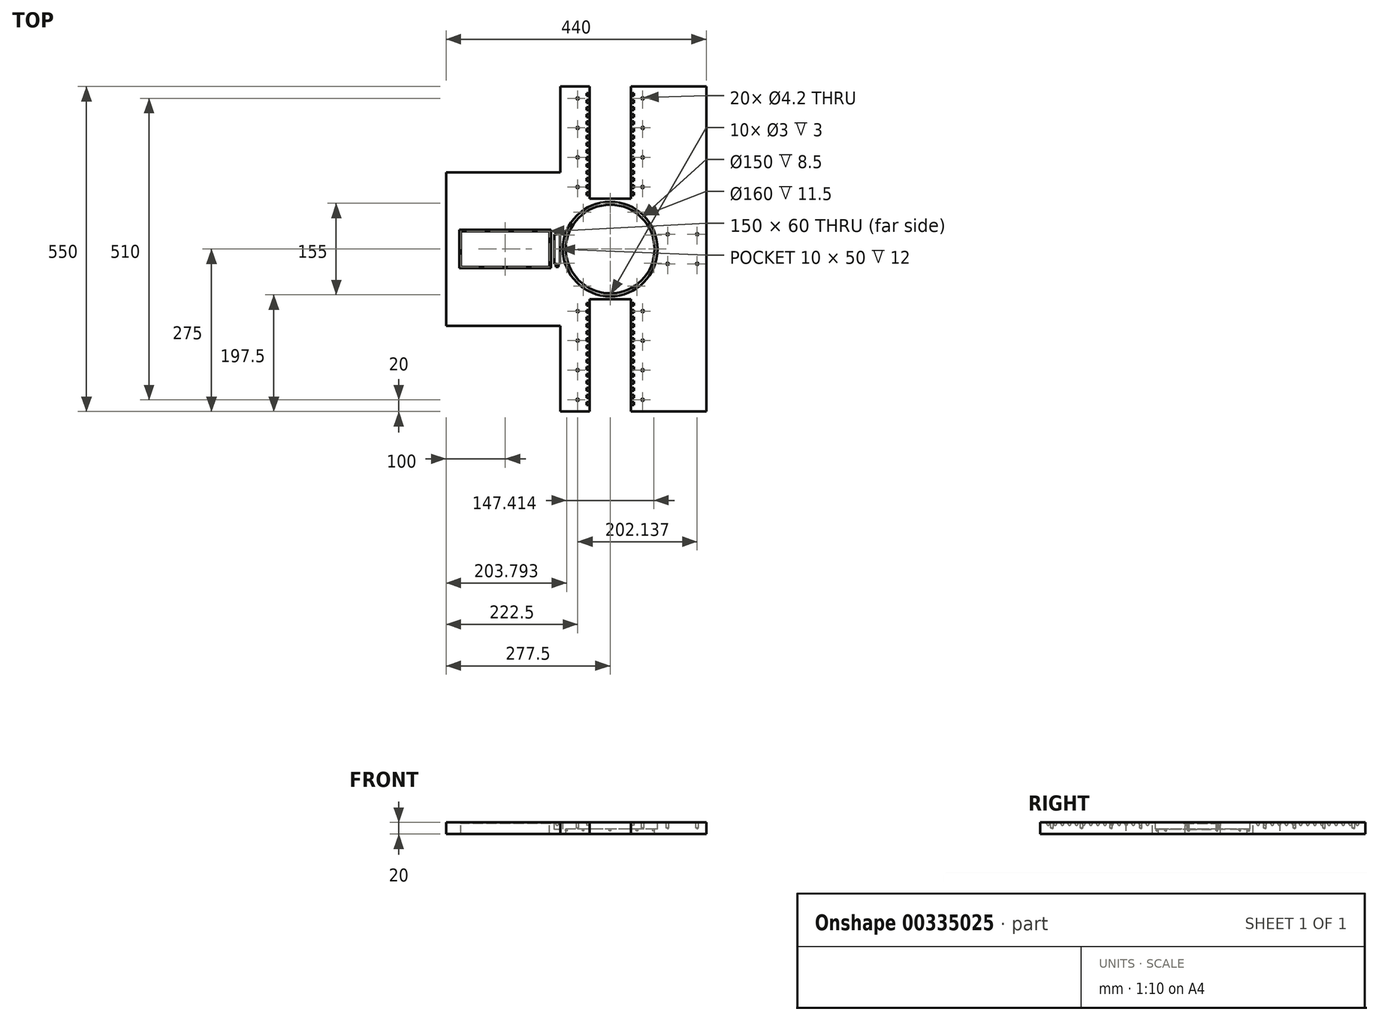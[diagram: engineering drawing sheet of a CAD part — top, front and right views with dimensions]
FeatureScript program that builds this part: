
annotation { "Feature Type Name" : "Feature", "Feature Type Description" : "" }
export const myFeature = defineFeature(function(context is Context, id is Id, definition is map)
    precondition{}
    {
        {
            var Q0;
            Q0=qCreatedBy(makeId("Top.planeOp"),FACE);
            var sketch = newSketch(context, id + "F0", { "sketchPlane" : qUnion([Q0])});
            skLineSegment(sketch, "E0.bottom", {"start": v(100, -127.5) * mm, "end": v(-100, -127.5) * mm});
            skLineSegment(sketch, "E0.top", {"start": v(100, 127.5) * mm, "end": v(-100, 127.5) * mm});
            skLineSegment(sketch, "E0.left", {"start": v(100, -127.5) * mm, "end": v(100, 127.5) * mm});
            skLineSegment(sketch, "E0.right", {"start": v(-100, -127.5) * mm, "end": v(-100, 127.5) * mm});
            skPoint(sketch, "E0.middle", {"position": v(0, 0) * mm});
            skSolve(sketch);
        }
        {
            var Q0;
            Q0 = qSketchRegion(id + "F0", true);
            extrude(context, id + "F1", {"entities" : qUnion([Q0]), "depth" : 20 * mm});
        }
        {
            var Q0;
            Q0=makeQuery(id+"F1.opExtrude","CAP_FACE",FACE,{"disambiguationData":[OSD([sQuery(id+"F0.wireOp",EDGE,"E0.bottom"),sQuery(id+"F0.wireOp",EDGE,"E0.top"),sQuery(id+"F0.wireOp",EDGE,"E0.left"),sQuery(id+"F0.wireOp",EDGE,"E0.right")])],"isStart":false});
            var sketch = newSketch(context, id + "F2", { "sketchPlane" : qUnion([Q0])});
            skLineSegment(sketch, "E1.bottom", {"start": v(75, -30) * mm, "end": v(-75, -30) * mm});
            skLineSegment(sketch, "E1.top", {"start": v(75, 30) * mm, "end": v(-75, 30) * mm});
            skLineSegment(sketch, "E1.left", {"start": v(75, -30) * mm, "end": v(75, 30) * mm});
            skLineSegment(sketch, "E1.right", {"start": v(-75, -30) * mm, "end": v(-75, 30) * mm});
            skPoint(sketch, "E1.middle", {"position": v(0, 0) * mm});
            skSolve(sketch);
        }
        {
            var Q0;
            Q0=makeQuery(id+"F2.imprint","IMPRINT",FACE,{"disambiguationData":[TD([[makeQuery(id+"F2.imprint","IMPRINT",EDGE,{"derivedFrom":sQuery(id+"F2.wireOp",EDGE,"E1.bottom")}),-1.0]])]});
            extrude(context, id + "F3", {"entities" : qUnion([Q0]), "operationType" : NewBodyOperationType.REMOVE, "endBound" : BoundingType.THROUGH_ALL, "oppositeDirection" : true, "depth" : 25 * mm});
        }
        {
            var Q0;
            Q0=makeQuery(id+"F1.opExtrude","CAP_FACE",FACE,{"disambiguationData":[OSD([sQuery(id+"F0.wireOp",EDGE,"E0.bottom"),sQuery(id+"F0.wireOp",EDGE,"E0.top"),sQuery(id+"F0.wireOp",EDGE,"E0.left"),sQuery(id+"F0.wireOp",EDGE,"E0.right")])],"isStart":false});
            var sketch = newSketch(context, id + "F4", { "sketchPlane" : qUnion([Q0])});
            skLineSegment(sketch, "E2.bottom", {"start": v(77.5, -32.5) * mm, "end": v(-77.5, -32.5) * mm});
            skLineSegment(sketch, "E2.top", {"start": v(77.5, 32.5) * mm, "end": v(-77.5, 32.5) * mm});
            skLineSegment(sketch, "E2.left", {"start": v(77.5, -32.5) * mm, "end": v(77.5, 32.5) * mm});
            skLineSegment(sketch, "E2.right", {"start": v(-77.5, -32.5) * mm, "end": v(-77.5, 32.5) * mm});
            skPoint(sketch, "E2.middle", {"position": v(0, 0) * mm});
            skSolve(sketch);
        }
        {
            var Q0;
            Q0=makeQuery(id+"F4.imprint","IMPRINT",FACE,{"disambiguationData":[TD([[makeQuery(id+"F4.imprint","IMPRINT",EDGE,{"derivedFrom":sQuery(id+"F4.wireOp",EDGE,"E2.bottom")}),-1.0]])]});
            extrude(context, id + "F5", {"entities" : qUnion([Q0]), "operationType" : NewBodyOperationType.REMOVE, "oppositeDirection" : true, "depth" : 2 * mm});
        }
        {
            var Q0;
            Q0=makeQuery(id+"F1.opExtrude","SWEPT_FACE",FACE,{"disambiguationData":[OSD([sQuery(id+"F0.wireOp",EDGE,"E0.left")])]});
            extrude(context, id + "F6", {"entities" : qUnion([Q0]), "operationType" : NewBodyOperationType.ADD, "depth" : 240 * mm});
        }
        {
            var Q0;
            {var subQ0=sQuery(id+"F0.wireOp",EDGE,"E0.left");Q0=makeQuery(id+"F6.boolean.opBoolean","MERGE",FACE,{"derivedFrom":[makeQuery(id+"F1.opExtrude","CAP_FACE",FACE,{"disambiguationData":[OSD([sQuery(id+"F0.wireOp",EDGE,"E0.bottom"),sQuery(id+"F0.wireOp",EDGE,"E0.top"),subQ0,sQuery(id+"F0.wireOp",EDGE,"E0.right")])],"isStart":false}),makeQuery(id+"F6.opExtrude","SWEPT_FACE",FACE,{"disambiguationData":[OSD([subQ0]),TDD([makeQuery(id+"F1.opExtrude","CAP_EDGE",EDGE,{"disambiguationData":[OSD([subQ0])],"isStart":false})])]})]});}
            var sketch = newSketch(context, id + "F7", { "sketchPlane" : qUnion([Q0])});
            skCircle(sketch, "E3", {"center": v(177.5, 0) * mm, "radius": 80 * mm});
            skCircle(sketch, "E4", {"center": v(177.5, 0) * mm, "radius": 75 * mm});
            skSolve(sketch);
        }
        {
            var Q0;
            Q0=makeQuery(id+"F7.imprint","IMPRINT",FACE,{"disambiguationData":[TD([[makeQuery(id+"F7.imprint","IMPRINT",EDGE,{"derivedFrom":sQuery(id+"F7.wireOp",EDGE,"E4")}),1.0]])]});
            extrude(context, id + "F8", {"entities" : qUnion([Q0]), "operationType" : NewBodyOperationType.REMOVE, "oppositeDirection" : true, "depth" : 25 * mm});
        }
        {
            var Q0;
            Q0 = qSketchRegion(id + "F7", true);
            extrude(context, id + "F9", {"entities" : qUnion([Q0]), "operationType" : NewBodyOperationType.REMOVE, "oppositeDirection" : true, "depth" : 11.5 * mm});
        }
        {
            var Q0;
            {var subQ0=sQuery(id+"F0.wireOp",EDGE,"E0.left");Q0=makeQuery(id+"F6.boolean.opBoolean","MERGE",FACE,{"derivedFrom":[makeQuery(id+"F1.opExtrude","CAP_FACE",FACE,{"disambiguationData":[OSD([sQuery(id+"F0.wireOp",EDGE,"E0.bottom"),sQuery(id+"F0.wireOp",EDGE,"E0.top"),subQ0,sQuery(id+"F0.wireOp",EDGE,"E0.right")])],"isStart":false}),makeQuery(id+"F6.opExtrude","SWEPT_FACE",FACE,{"disambiguationData":[OSD([subQ0]),TDD([makeQuery(id+"F1.opExtrude","CAP_EDGE",EDGE,{"disambiguationData":[OSD([subQ0])],"isStart":false})])]})]});}
            var sketch = newSketch(context, id + "F10", { "sketchPlane" : qUnion([Q0])});
            skLineSegment(sketch, "E5.bottom", {"start": v(262.5, -275) * mm, "end": v(92.5, -275) * mm});
            skLineSegment(sketch, "E5.top", {"start": v(262.5, 275) * mm, "end": v(92.5, 275) * mm});
            skLineSegment(sketch, "E5.left", {"start": v(262.5, -275) * mm, "end": v(262.5, 275) * mm});
            skLineSegment(sketch, "E5.right", {"start": v(92.5, -275) * mm, "end": v(92.5, 275) * mm});
            skPoint(sketch, "E5.middle", {"position": v(177.5, 0) * mm});
            skSolve(sketch);
        }
        {
            var Q0;
            {var subQ0=sQuery(id+"F10.wireOp",EDGE,"E5.bottom");Q0=makeQuery(id+"F10.imprint","IMPRINT",FACE,{"disambiguationData":[TD([[makeQuery(id+"F10.imprint","IMPRINT",EDGE,{"derivedFrom":subQ0}),-1.0]])]});}
            var Q1;
            {var subQ0=sQuery(id+"F10.wireOp",EDGE,"E5.top");Q1=makeQuery(id+"F10.imprint","IMPRINT",FACE,{"disambiguationData":[TD([[makeQuery(id+"F10.imprint","IMPRINT",EDGE,{"derivedFrom":subQ0}),1.0]])]});}
            var Q2;
            Q2=makeQuery(id+"F10.imprint","IMPRINT",FACE,{"disambiguationData":[TD([[makeQuery(id+"F10.imprint","IMPRINT",EDGE,{"derivedFrom":makeQuery(id+"F9.boolean.opBoolean","COPY",EDGE,{"derivedFrom":makeQuery(id+"F9.opExtrude","CAP_EDGE",EDGE,{"disambiguationData":[OSD([sQuery(id+"F7.wireOp",EDGE,"E3")])],"isStart":true})})}),-1.0]])]});
            extrude(context, id + "F11", {"entities" : qUnion([Q0, Q1, Q2]), "operationType" : NewBodyOperationType.ADD, "oppositeDirection" : true, "depth" : 10 * mm});
        }
        {
            var Q0;
            {var subQ0=sQuery(id+"F0.wireOp",EDGE,"E0.left");Q0=makeQuery(id+"F11.boolean.opBoolean","MERGE",FACE,{"derivedFrom":[makeQuery(id+"F6.boolean.opBoolean","MERGE",FACE,{"derivedFrom":[makeQuery(id+"F1.opExtrude","CAP_FACE",FACE,{"disambiguationData":[OSD([sQuery(id+"F0.wireOp",EDGE,"E0.bottom"),sQuery(id+"F0.wireOp",EDGE,"E0.top"),subQ0,sQuery(id+"F0.wireOp",EDGE,"E0.right")])],"isStart":false}),makeQuery(id+"F6.opExtrude","SWEPT_FACE",FACE,{"disambiguationData":[OSD([subQ0]),TDD([makeQuery(id+"F1.opExtrude","CAP_EDGE",EDGE,{"disambiguationData":[OSD([subQ0])],"isStart":false})])]})]}),makeQuery(id+"F11.opExtrude","CAP_FACE",FACE,{"disambiguationData":[OSD([sQuery(id+"F7.wireOp",EDGE,"E3"),sQuery(id+"F10.wireOp",EDGE,"E5.bottom"),sQuery(id+"F10.wireOp",EDGE,"E5.top"),sQuery(id+"F10.wireOp",EDGE,"E5.left"),sQuery(id+"F10.wireOp",EDGE,"E5.right")])],"isStart":true})]});}
            var sketch = newSketch(context, id + "F12", { "sketchPlane" : qUnion([Q0])});
            skLineSegment(sketch, "E6.bottom", {"start": v(212.5, 85) * mm, "end": v(142.5, 85) * mm});
            skLineSegment(sketch, "E6.top", {"start": v(212.5, 465) * mm, "end": v(142.5, 465) * mm});
            skLineSegment(sketch, "E6.left", {"start": v(212.5, 85) * mm, "end": v(212.5, 465) * mm});
            skLineSegment(sketch, "E6.right", {"start": v(142.5, 85) * mm, "end": v(142.5, 465) * mm});
            skPoint(sketch, "E6.middle", {"position": v(177.5, 275) * mm});
            skSolve(sketch);
        }
        {
            var Q0;
            {var subQ0=sQuery(id+"F12.wireOp",EDGE,"E6.bottom");Q0=makeQuery(id+"F12.imprint","IMPRINT",FACE,{"disambiguationData":[TD([[makeQuery(id+"F12.imprint","IMPRINT",EDGE,{"derivedFrom":subQ0}),-1.0]])]});}
            extrude(context, id + "F13", {"entities" : qUnion([Q0]), "operationType" : NewBodyOperationType.REMOVE, "oppositeDirection" : true, "depth" : 25 * mm});
        }
        {
            var Q0;
            {var subQ0=sQuery(id+"F0.wireOp",EDGE,"E0.left");Q0=makeQuery(id+"F11.boolean.opBoolean","MERGE",FACE,{"derivedFrom":[makeQuery(id+"F6.boolean.opBoolean","MERGE",FACE,{"derivedFrom":[makeQuery(id+"F1.opExtrude","CAP_FACE",FACE,{"disambiguationData":[OSD([sQuery(id+"F0.wireOp",EDGE,"E0.bottom"),sQuery(id+"F0.wireOp",EDGE,"E0.top"),subQ0,sQuery(id+"F0.wireOp",EDGE,"E0.right")])],"isStart":false}),makeQuery(id+"F6.opExtrude","SWEPT_FACE",FACE,{"disambiguationData":[OSD([subQ0]),TDD([makeQuery(id+"F1.opExtrude","CAP_EDGE",EDGE,{"disambiguationData":[OSD([subQ0])],"isStart":false})])]})]}),makeQuery(id+"F11.opExtrude","CAP_FACE",FACE,{"disambiguationData":[OSD([sQuery(id+"F7.wireOp",EDGE,"E3"),sQuery(id+"F10.wireOp",EDGE,"E5.bottom"),sQuery(id+"F10.wireOp",EDGE,"E5.top"),sQuery(id+"F10.wireOp",EDGE,"E5.left"),sQuery(id+"F10.wireOp",EDGE,"E5.right")])],"isStart":true})]});}
            var sketch = newSketch(context, id + "F14", { "sketchPlane" : qUnion([Q0])});
            skLineSegment(sketch, "E7.bottom", {"start": v(217.5, 91) * mm, "end": v(137.5, 91) * mm});
            skLineSegment(sketch, "E7.top", {"start": v(217.5, 96) * mm, "end": v(137.5, 96) * mm});
            skLineSegment(sketch, "E7.left", {"start": v(217.5, 91) * mm, "end": v(217.5, 96) * mm});
            skLineSegment(sketch, "E7.right", {"start": v(137.5, 91) * mm, "end": v(137.5, 96) * mm});
            skPoint(sketch, "E7.middle", {"position": v(177.5, 93.5) * mm});
            skPoint(sketch, "E7.middle.positionSnap0", {"position": v(177.5, 85) * mm});
            skPoint(sketch, "E7.centerSnap0", {"position": v(177.5, 85) * mm});
            skLineSegment(sketch, "E8.0.1.0", {"start": v(217.5, 108) * mm, "end": v(137.5, 108) * mm});
            skLineSegment(sketch, "E8.0.1.1", {"start": v(217.5, 103) * mm, "end": v(137.5, 103) * mm});
            skLineSegment(sketch, "E8.0.1.2", {"start": v(217.5, 103) * mm, "end": v(217.5, 108) * mm});
            skLineSegment(sketch, "E8.0.1.3", {"start": v(137.5, 103) * mm, "end": v(137.5, 108) * mm});
            skPoint(sketch, "E8.0.1.4", {"position": v(177.5, 105.5) * mm});
            skLineSegment(sketch, "E8.0.2.0", {"start": v(217.5, 120) * mm, "end": v(137.5, 120) * mm});
            skLineSegment(sketch, "E8.0.2.1", {"start": v(217.5, 115) * mm, "end": v(137.5, 115) * mm});
            skLineSegment(sketch, "E8.0.2.2", {"start": v(217.5, 115) * mm, "end": v(217.5, 120) * mm});
            skLineSegment(sketch, "E8.0.2.3", {"start": v(137.5, 115) * mm, "end": v(137.5, 120) * mm});
            skPoint(sketch, "E8.0.2.4", {"position": v(177.5, 117.5) * mm});
            skLineSegment(sketch, "E8.0.3.0", {"start": v(217.5, 132) * mm, "end": v(137.5, 132) * mm});
            skLineSegment(sketch, "E8.0.3.1", {"start": v(217.5, 127) * mm, "end": v(137.5, 127) * mm});
            skLineSegment(sketch, "E8.0.3.2", {"start": v(217.5, 127) * mm, "end": v(217.5, 132) * mm});
            skLineSegment(sketch, "E8.0.3.3", {"start": v(137.5, 127) * mm, "end": v(137.5, 132) * mm});
            skPoint(sketch, "E8.0.3.4", {"position": v(177.5, 129.5) * mm});
            skLineSegment(sketch, "E8.0.4.0", {"start": v(217.5, 144) * mm, "end": v(137.5, 144) * mm});
            skLineSegment(sketch, "E8.0.4.1", {"start": v(217.5, 139) * mm, "end": v(137.5, 139) * mm});
            skLineSegment(sketch, "E8.0.4.2", {"start": v(217.5, 139) * mm, "end": v(217.5, 144) * mm});
            skLineSegment(sketch, "E8.0.4.3", {"start": v(137.5, 139) * mm, "end": v(137.5, 144) * mm});
            skPoint(sketch, "E8.0.4.4", {"position": v(177.5, 141.5) * mm});
            skLineSegment(sketch, "E8.0.5.0", {"start": v(217.5, 156) * mm, "end": v(137.5, 156) * mm});
            skLineSegment(sketch, "E8.0.5.1", {"start": v(217.5, 151) * mm, "end": v(137.5, 151) * mm});
            skLineSegment(sketch, "E8.0.5.2", {"start": v(217.5, 151) * mm, "end": v(217.5, 156) * mm});
            skLineSegment(sketch, "E8.0.5.3", {"start": v(137.5, 151) * mm, "end": v(137.5, 156) * mm});
            skPoint(sketch, "E8.0.5.4", {"position": v(177.5, 153.5) * mm});
            skLineSegment(sketch, "E8.0.6.0", {"start": v(217.5, 168) * mm, "end": v(137.5, 168) * mm});
            skLineSegment(sketch, "E8.0.6.1", {"start": v(217.5, 163) * mm, "end": v(137.5, 163) * mm});
            skLineSegment(sketch, "E8.0.6.2", {"start": v(217.5, 163) * mm, "end": v(217.5, 168) * mm});
            skLineSegment(sketch, "E8.0.6.3", {"start": v(137.5, 163) * mm, "end": v(137.5, 168) * mm});
            skPoint(sketch, "E8.0.6.4", {"position": v(177.5, 165.5) * mm});
            skLineSegment(sketch, "E8.0.7.0", {"start": v(217.5, 180) * mm, "end": v(137.5, 180) * mm});
            skLineSegment(sketch, "E8.0.7.1", {"start": v(217.5, 175) * mm, "end": v(137.5, 175) * mm});
            skLineSegment(sketch, "E8.0.7.2", {"start": v(217.5, 175) * mm, "end": v(217.5, 180) * mm});
            skLineSegment(sketch, "E8.0.7.3", {"start": v(137.5, 175) * mm, "end": v(137.5, 180) * mm});
            skPoint(sketch, "E8.0.7.4", {"position": v(177.5, 177.5) * mm});
            skLineSegment(sketch, "E8.0.8.0", {"start": v(217.5, 192) * mm, "end": v(137.5, 192) * mm});
            skLineSegment(sketch, "E8.0.8.1", {"start": v(217.5, 187) * mm, "end": v(137.5, 187) * mm});
            skLineSegment(sketch, "E8.0.8.2", {"start": v(217.5, 187) * mm, "end": v(217.5, 192) * mm});
            skLineSegment(sketch, "E8.0.8.3", {"start": v(137.5, 187) * mm, "end": v(137.5, 192) * mm});
            skPoint(sketch, "E8.0.8.4", {"position": v(177.5, 189.5) * mm});
            skLineSegment(sketch, "E8.0.9.0", {"start": v(217.5, 204) * mm, "end": v(137.5, 204) * mm});
            skLineSegment(sketch, "E8.0.9.1", {"start": v(217.5, 199) * mm, "end": v(137.5, 199) * mm});
            skLineSegment(sketch, "E8.0.9.2", {"start": v(217.5, 199) * mm, "end": v(217.5, 204) * mm});
            skLineSegment(sketch, "E8.0.9.3", {"start": v(137.5, 199) * mm, "end": v(137.5, 204) * mm});
            skPoint(sketch, "E8.0.9.4", {"position": v(177.5, 201.5) * mm});
            skLineSegment(sketch, "E8.0.10.0", {"start": v(217.5, 216) * mm, "end": v(137.5, 216) * mm});
            skLineSegment(sketch, "E8.0.10.1", {"start": v(217.5, 211) * mm, "end": v(137.5, 211) * mm});
            skLineSegment(sketch, "E8.0.10.2", {"start": v(217.5, 211) * mm, "end": v(217.5, 216) * mm});
            skLineSegment(sketch, "E8.0.10.3", {"start": v(137.5, 211) * mm, "end": v(137.5, 216) * mm});
            skPoint(sketch, "E8.0.10.4", {"position": v(177.5, 213.5) * mm});
            skLineSegment(sketch, "E8.0.11.0", {"start": v(217.5, 228) * mm, "end": v(137.5, 228) * mm});
            skLineSegment(sketch, "E8.0.11.1", {"start": v(217.5, 223) * mm, "end": v(137.5, 223) * mm});
            skLineSegment(sketch, "E8.0.11.2", {"start": v(217.5, 223) * mm, "end": v(217.5, 228) * mm});
            skLineSegment(sketch, "E8.0.11.3", {"start": v(137.5, 223) * mm, "end": v(137.5, 228) * mm});
            skPoint(sketch, "E8.0.11.4", {"position": v(177.5, 225.5) * mm});
            skLineSegment(sketch, "E8.0.12.0", {"start": v(217.5, 240) * mm, "end": v(137.5, 240) * mm});
            skLineSegment(sketch, "E8.0.12.1", {"start": v(217.5, 235) * mm, "end": v(137.5, 235) * mm});
            skLineSegment(sketch, "E8.0.12.2", {"start": v(217.5, 235) * mm, "end": v(217.5, 240) * mm});
            skLineSegment(sketch, "E8.0.12.3", {"start": v(137.5, 235) * mm, "end": v(137.5, 240) * mm});
            skPoint(sketch, "E8.0.12.4", {"position": v(177.5, 237.5) * mm});
            skLineSegment(sketch, "E8.0.13.0", {"start": v(217.5, 252) * mm, "end": v(137.5, 252) * mm});
            skLineSegment(sketch, "E8.0.13.1", {"start": v(217.5, 247) * mm, "end": v(137.5, 247) * mm});
            skLineSegment(sketch, "E8.0.13.2", {"start": v(217.5, 247) * mm, "end": v(217.5, 252) * mm});
            skLineSegment(sketch, "E8.0.13.3", {"start": v(137.5, 247) * mm, "end": v(137.5, 252) * mm});
            skPoint(sketch, "E8.0.13.4", {"position": v(177.5, 249.5) * mm});
            skLineSegment(sketch, "E8.0.14.0", {"start": v(217.5, 264) * mm, "end": v(137.5, 264) * mm});
            skLineSegment(sketch, "E8.0.14.1", {"start": v(217.5, 259) * mm, "end": v(137.5, 259) * mm});
            skLineSegment(sketch, "E8.0.14.2", {"start": v(217.5, 259) * mm, "end": v(217.5, 264) * mm});
            skLineSegment(sketch, "E8.0.14.3", {"start": v(137.5, 259) * mm, "end": v(137.5, 264) * mm});
            skPoint(sketch, "E8.0.14.4", {"position": v(177.5, 261.5) * mm});
            skLineSegment(sketch, "E8.direction1", {"start": v(137.5, 91) * mm, "end": v(162.5, 91) * mm, "construction": true});
            skLineSegment(sketch, "E8.direction2", {"start": v(137.5, 91) * mm, "end": v(137.5, 103) * mm, "construction": true});
            skLineSegment(sketch, "E9.bottom", {"start": v(142.5, -85) * mm, "end": v(212.5, -85) * mm});
            skLineSegment(sketch, "E9.top", {"start": v(142.5, -290.73) * mm, "end": v(212.5, -290.73) * mm});
            skLineSegment(sketch, "E9.left", {"start": v(142.5, -85) * mm, "end": v(142.5, -290.73) * mm});
            skLineSegment(sketch, "E9.right", {"start": v(212.5, -85) * mm, "end": v(212.5, -290.73) * mm});
            skLineSegment(sketch, "E10.bottom", {"start": v(137.5, -91) * mm, "end": v(217.5, -91) * mm});
            skLineSegment(sketch, "E10.top", {"start": v(137.5, -96) * mm, "end": v(217.5, -96) * mm});
            skLineSegment(sketch, "E10.left", {"start": v(137.5, -91) * mm, "end": v(137.5, -96) * mm});
            skLineSegment(sketch, "E10.right", {"start": v(217.5, -91) * mm, "end": v(217.5, -96) * mm});
            skLineSegment(sketch, "E11.0.1.0", {"start": v(137.5, -103) * mm, "end": v(217.5, -103) * mm});
            skLineSegment(sketch, "E11.0.1.1", {"start": v(137.5, -108) * mm, "end": v(217.5, -108) * mm});
            skLineSegment(sketch, "E11.0.1.2", {"start": v(137.5, -103) * mm, "end": v(137.5, -108) * mm});
            skLineSegment(sketch, "E11.0.1.3", {"start": v(217.5, -103) * mm, "end": v(217.5, -108) * mm});
            skLineSegment(sketch, "E11.0.2.0", {"start": v(137.5, -115) * mm, "end": v(217.5, -115) * mm});
            skLineSegment(sketch, "E11.0.2.1", {"start": v(137.5, -120) * mm, "end": v(217.5, -120) * mm});
            skLineSegment(sketch, "E11.0.2.2", {"start": v(137.5, -115) * mm, "end": v(137.5, -120) * mm});
            skLineSegment(sketch, "E11.0.2.3", {"start": v(217.5, -115) * mm, "end": v(217.5, -120) * mm});
            skLineSegment(sketch, "E11.0.3.0", {"start": v(137.5, -127) * mm, "end": v(217.5, -127) * mm});
            skLineSegment(sketch, "E11.0.3.1", {"start": v(137.5, -132) * mm, "end": v(217.5, -132) * mm});
            skLineSegment(sketch, "E11.0.3.2", {"start": v(137.5, -127) * mm, "end": v(137.5, -132) * mm});
            skLineSegment(sketch, "E11.0.3.3", {"start": v(217.5, -127) * mm, "end": v(217.5, -132) * mm});
            skLineSegment(sketch, "E11.0.4.0", {"start": v(137.5, -139) * mm, "end": v(217.5, -139) * mm});
            skLineSegment(sketch, "E11.0.4.1", {"start": v(137.5, -144) * mm, "end": v(217.5, -144) * mm});
            skLineSegment(sketch, "E11.0.4.2", {"start": v(137.5, -139) * mm, "end": v(137.5, -144) * mm});
            skLineSegment(sketch, "E11.0.4.3", {"start": v(217.5, -139) * mm, "end": v(217.5, -144) * mm});
            skLineSegment(sketch, "E11.0.5.0", {"start": v(137.5, -151) * mm, "end": v(217.5, -151) * mm});
            skLineSegment(sketch, "E11.0.5.1", {"start": v(137.5, -156) * mm, "end": v(217.5, -156) * mm});
            skLineSegment(sketch, "E11.0.5.2", {"start": v(137.5, -151) * mm, "end": v(137.5, -156) * mm});
            skLineSegment(sketch, "E11.0.5.3", {"start": v(217.5, -151) * mm, "end": v(217.5, -156) * mm});
            skLineSegment(sketch, "E11.0.6.0", {"start": v(137.5, -163) * mm, "end": v(217.5, -163) * mm});
            skLineSegment(sketch, "E11.0.6.1", {"start": v(137.5, -168) * mm, "end": v(217.5, -168) * mm});
            skLineSegment(sketch, "E11.0.6.2", {"start": v(137.5, -163) * mm, "end": v(137.5, -168) * mm});
            skLineSegment(sketch, "E11.0.6.3", {"start": v(217.5, -163) * mm, "end": v(217.5, -168) * mm});
            skLineSegment(sketch, "E11.0.7.0", {"start": v(137.5, -175) * mm, "end": v(217.5, -175) * mm});
            skLineSegment(sketch, "E11.0.7.1", {"start": v(137.5, -180) * mm, "end": v(217.5, -180) * mm});
            skLineSegment(sketch, "E11.0.7.2", {"start": v(137.5, -175) * mm, "end": v(137.5, -180) * mm});
            skLineSegment(sketch, "E11.0.7.3", {"start": v(217.5, -175) * mm, "end": v(217.5, -180) * mm});
            skLineSegment(sketch, "E11.0.8.0", {"start": v(137.5, -187) * mm, "end": v(217.5, -187) * mm});
            skLineSegment(sketch, "E11.0.8.1", {"start": v(137.5, -192) * mm, "end": v(217.5, -192) * mm});
            skLineSegment(sketch, "E11.0.8.2", {"start": v(137.5, -187) * mm, "end": v(137.5, -192) * mm});
            skLineSegment(sketch, "E11.0.8.3", {"start": v(217.5, -187) * mm, "end": v(217.5, -192) * mm});
            skLineSegment(sketch, "E11.0.9.0", {"start": v(137.5, -199) * mm, "end": v(217.5, -199) * mm});
            skLineSegment(sketch, "E11.0.9.1", {"start": v(137.5, -204) * mm, "end": v(217.5, -204) * mm});
            skLineSegment(sketch, "E11.0.9.2", {"start": v(137.5, -199) * mm, "end": v(137.5, -204) * mm});
            skLineSegment(sketch, "E11.0.9.3", {"start": v(217.5, -199) * mm, "end": v(217.5, -204) * mm});
            skLineSegment(sketch, "E11.0.10.0", {"start": v(137.5, -211) * mm, "end": v(217.5, -211) * mm});
            skLineSegment(sketch, "E11.0.10.1", {"start": v(137.5, -216) * mm, "end": v(217.5, -216) * mm});
            skLineSegment(sketch, "E11.0.10.2", {"start": v(137.5, -211) * mm, "end": v(137.5, -216) * mm});
            skLineSegment(sketch, "E11.0.10.3", {"start": v(217.5, -211) * mm, "end": v(217.5, -216) * mm});
            skLineSegment(sketch, "E11.0.11.0", {"start": v(137.5, -223) * mm, "end": v(217.5, -223) * mm});
            skLineSegment(sketch, "E11.0.11.1", {"start": v(137.5, -228) * mm, "end": v(217.5, -228) * mm});
            skLineSegment(sketch, "E11.0.11.2", {"start": v(137.5, -223) * mm, "end": v(137.5, -228) * mm});
            skLineSegment(sketch, "E11.0.11.3", {"start": v(217.5, -223) * mm, "end": v(217.5, -228) * mm});
            skLineSegment(sketch, "E11.0.12.0", {"start": v(137.5, -235) * mm, "end": v(217.5, -235) * mm});
            skLineSegment(sketch, "E11.0.12.1", {"start": v(137.5, -240) * mm, "end": v(217.5, -240) * mm});
            skLineSegment(sketch, "E11.0.12.2", {"start": v(137.5, -235) * mm, "end": v(137.5, -240) * mm});
            skLineSegment(sketch, "E11.0.12.3", {"start": v(217.5, -235) * mm, "end": v(217.5, -240) * mm});
            skLineSegment(sketch, "E11.0.13.0", {"start": v(137.5, -247) * mm, "end": v(217.5, -247) * mm});
            skLineSegment(sketch, "E11.0.13.1", {"start": v(137.5, -252) * mm, "end": v(217.5, -252) * mm});
            skLineSegment(sketch, "E11.0.13.2", {"start": v(137.5, -247) * mm, "end": v(137.5, -252) * mm});
            skLineSegment(sketch, "E11.0.13.3", {"start": v(217.5, -247) * mm, "end": v(217.5, -252) * mm});
            skLineSegment(sketch, "E11.0.14.0", {"start": v(137.5, -259) * mm, "end": v(217.5, -259) * mm});
            skLineSegment(sketch, "E11.0.14.1", {"start": v(137.5, -264) * mm, "end": v(217.5, -264) * mm});
            skLineSegment(sketch, "E11.0.14.2", {"start": v(137.5, -259) * mm, "end": v(137.5, -264) * mm});
            skLineSegment(sketch, "E11.0.14.3", {"start": v(217.5, -259) * mm, "end": v(217.5, -264) * mm});
            skLineSegment(sketch, "E11.direction1", {"start": v(137.5, -96) * mm, "end": v(162.5, -96) * mm, "construction": true});
            skLineSegment(sketch, "E11.direction2", {"start": v(137.5, -96) * mm, "end": v(137.5, -108) * mm, "construction": true});
            skSolve(sketch);
        }
        {
            var Q0;
            {var subQ0=sQuery(id+"F0.wireOp",EDGE,"E0.left");Q0=makeQuery(id+"F11.boolean.opBoolean","MERGE",FACE,{"derivedFrom":[makeQuery(id+"F6.boolean.opBoolean","MERGE",FACE,{"derivedFrom":[makeQuery(id+"F1.opExtrude","CAP_FACE",FACE,{"disambiguationData":[OSD([sQuery(id+"F0.wireOp",EDGE,"E0.bottom"),sQuery(id+"F0.wireOp",EDGE,"E0.top"),subQ0,sQuery(id+"F0.wireOp",EDGE,"E0.right")])],"isStart":false}),makeQuery(id+"F6.opExtrude","SWEPT_FACE",FACE,{"disambiguationData":[OSD([subQ0]),TDD([makeQuery(id+"F1.opExtrude","CAP_EDGE",EDGE,{"disambiguationData":[OSD([subQ0])],"isStart":false})])]})]}),makeQuery(id+"F11.opExtrude","CAP_FACE",FACE,{"disambiguationData":[OSD([sQuery(id+"F7.wireOp",EDGE,"E3"),sQuery(id+"F10.wireOp",EDGE,"E5.bottom"),sQuery(id+"F10.wireOp",EDGE,"E5.top"),sQuery(id+"F10.wireOp",EDGE,"E5.left"),sQuery(id+"F10.wireOp",EDGE,"E5.right")])],"isStart":true})]});}
            var sketch = newSketch(context, id + "F15", { "sketchPlane" : qUnion([Q0])});
            skLineSegment(sketch, "E12.bottom", {"start": v(142.5, -85) * mm, "end": v(212.5, -85) * mm});
            skLineSegment(sketch, "E12.top", {"start": v(142.5, -275) * mm, "end": v(212.5, -275) * mm});
            skLineSegment(sketch, "E12.left", {"start": v(142.5, -85) * mm, "end": v(142.5, -275) * mm});
            skLineSegment(sketch, "E12.right", {"start": v(212.5, -85) * mm, "end": v(212.5, -275) * mm});
            skSolve(sketch);
        }
        {
            var Q0;
            Q0=makeQuery(id+"F15.imprint","IMPRINT",FACE,{"disambiguationData":[TD([[makeQuery(id+"F15.imprint","IMPRINT",EDGE,{"derivedFrom":sQuery(id+"F15.wireOp",EDGE,"E12.bottom")}),-1.0]])]});
            extrude(context, id + "F16", {"entities" : qUnion([Q0]), "operationType" : NewBodyOperationType.REMOVE, "oppositeDirection" : true, "depth" : 25 * mm});
        }
        {
            var Q0;
            Q0 = qSketchRegion(id + "F14", true);
            extrude(context, id + "F17", {"entities" : qUnion([Q0]), "operationType" : NewBodyOperationType.REMOVE, "oppositeDirection" : true, "depth" : 5 * mm});
        }
        {
            var Q0;
            {var subQ0=sQuery(id+"F14.wireOp",EDGE,"E8.0.14.0");Q0=makeQuery(id+"F17.boolean.opBoolean","COPY",EDGE,{"disambiguationData":[TD([makeQuery(id+"F13.boolean.opBoolean","COPY",FACE,{"derivedFrom":makeQuery(id+"F13.opExtrude","SWEPT_FACE",FACE,{"disambiguationData":[OSD([sQuery(id+"F12.wireOp",EDGE,"E6.right")])]})})])],"derivedFrom":makeQuery(id+"F17.opExtrude","CAP_EDGE",EDGE,{"disambiguationData":[OSD([subQ0])],"isStart":false})});}
            var Q1;
            {var subQ1=sQuery(id+"F14.wireOp",EDGE,"E8.0.14.1");Q1=makeQuery(id+"F17.boolean.opBoolean","COPY",EDGE,{"disambiguationData":[TD([makeQuery(id+"F13.boolean.opBoolean","COPY",FACE,{"derivedFrom":makeQuery(id+"F13.opExtrude","SWEPT_FACE",FACE,{"disambiguationData":[OSD([sQuery(id+"F12.wireOp",EDGE,"E6.right")])]})})])],"derivedFrom":makeQuery(id+"F17.opExtrude","CAP_EDGE",EDGE,{"disambiguationData":[OSD([subQ1])],"isStart":false})});}
            var Q2;
            {var subQ1=sQuery(id+"F14.wireOp",EDGE,"E8.0.13.0");Q2=makeQuery(id+"F17.boolean.opBoolean","COPY",EDGE,{"disambiguationData":[TD([makeQuery(id+"F13.boolean.opBoolean","COPY",FACE,{"derivedFrom":makeQuery(id+"F13.opExtrude","SWEPT_FACE",FACE,{"disambiguationData":[OSD([sQuery(id+"F12.wireOp",EDGE,"E6.right")])]})})])],"derivedFrom":makeQuery(id+"F17.opExtrude","CAP_EDGE",EDGE,{"disambiguationData":[OSD([subQ1])],"isStart":false})});}
            var Q3;
            {var subQ1=sQuery(id+"F14.wireOp",EDGE,"E8.0.13.1");Q3=makeQuery(id+"F17.boolean.opBoolean","COPY",EDGE,{"disambiguationData":[TD([makeQuery(id+"F13.boolean.opBoolean","COPY",FACE,{"derivedFrom":makeQuery(id+"F13.opExtrude","SWEPT_FACE",FACE,{"disambiguationData":[OSD([sQuery(id+"F12.wireOp",EDGE,"E6.right")])]})})])],"derivedFrom":makeQuery(id+"F17.opExtrude","CAP_EDGE",EDGE,{"disambiguationData":[OSD([subQ1])],"isStart":false})});}
            var Q4;
            {var subQ0=sQuery(id+"F14.wireOp",EDGE,"E8.0.12.1");Q4=makeQuery(id+"F17.boolean.opBoolean","COPY",EDGE,{"disambiguationData":[TD([makeQuery(id+"F13.boolean.opBoolean","COPY",FACE,{"derivedFrom":makeQuery(id+"F13.opExtrude","SWEPT_FACE",FACE,{"disambiguationData":[OSD([sQuery(id+"F12.wireOp",EDGE,"E6.right")])]})})])],"derivedFrom":makeQuery(id+"F17.opExtrude","CAP_EDGE",EDGE,{"disambiguationData":[OSD([subQ0])],"isStart":false})});}
            var Q5;
            {var subQ0=sQuery(id+"F14.wireOp",EDGE,"E8.0.12.0");Q5=makeQuery(id+"F17.boolean.opBoolean","COPY",EDGE,{"disambiguationData":[TD([makeQuery(id+"F13.boolean.opBoolean","COPY",FACE,{"derivedFrom":makeQuery(id+"F13.opExtrude","SWEPT_FACE",FACE,{"disambiguationData":[OSD([sQuery(id+"F12.wireOp",EDGE,"E6.right")])]})})])],"derivedFrom":makeQuery(id+"F17.opExtrude","CAP_EDGE",EDGE,{"disambiguationData":[OSD([subQ0])],"isStart":false})});}
            var Q6;
            {var subQ0=sQuery(id+"F14.wireOp",EDGE,"E8.0.11.0");Q6=makeQuery(id+"F17.boolean.opBoolean","COPY",EDGE,{"disambiguationData":[TD([makeQuery(id+"F13.boolean.opBoolean","COPY",FACE,{"derivedFrom":makeQuery(id+"F13.opExtrude","SWEPT_FACE",FACE,{"disambiguationData":[OSD([sQuery(id+"F12.wireOp",EDGE,"E6.right")])]})})])],"derivedFrom":makeQuery(id+"F17.opExtrude","CAP_EDGE",EDGE,{"disambiguationData":[OSD([subQ0])],"isStart":false})});}
            var Q7;
            {var subQ1=sQuery(id+"F14.wireOp",EDGE,"E8.0.11.1");Q7=makeQuery(id+"F17.boolean.opBoolean","COPY",EDGE,{"disambiguationData":[TD([makeQuery(id+"F13.boolean.opBoolean","COPY",FACE,{"derivedFrom":makeQuery(id+"F13.opExtrude","SWEPT_FACE",FACE,{"disambiguationData":[OSD([sQuery(id+"F12.wireOp",EDGE,"E6.right")])]})})])],"derivedFrom":makeQuery(id+"F17.opExtrude","CAP_EDGE",EDGE,{"disambiguationData":[OSD([subQ1])],"isStart":false})});}
            var Q8;
            {var subQ1=sQuery(id+"F14.wireOp",EDGE,"E8.0.10.1");Q8=makeQuery(id+"F17.boolean.opBoolean","COPY",EDGE,{"disambiguationData":[TD([makeQuery(id+"F13.boolean.opBoolean","COPY",FACE,{"derivedFrom":makeQuery(id+"F13.opExtrude","SWEPT_FACE",FACE,{"disambiguationData":[OSD([sQuery(id+"F12.wireOp",EDGE,"E6.right")])]})})])],"derivedFrom":makeQuery(id+"F17.opExtrude","CAP_EDGE",EDGE,{"disambiguationData":[OSD([subQ1])],"isStart":false})});}
            var Q9;
            {var subQ0=sQuery(id+"F14.wireOp",EDGE,"E8.0.10.0");Q9=makeQuery(id+"F17.boolean.opBoolean","COPY",EDGE,{"disambiguationData":[TD([makeQuery(id+"F13.boolean.opBoolean","COPY",FACE,{"derivedFrom":makeQuery(id+"F13.opExtrude","SWEPT_FACE",FACE,{"disambiguationData":[OSD([sQuery(id+"F12.wireOp",EDGE,"E6.right")])]})})])],"derivedFrom":makeQuery(id+"F17.opExtrude","CAP_EDGE",EDGE,{"disambiguationData":[OSD([subQ0])],"isStart":false})});}
            var Q10;
            {var subQ0=sQuery(id+"F14.wireOp",EDGE,"E8.0.9.0");Q10=makeQuery(id+"F17.boolean.opBoolean","COPY",EDGE,{"disambiguationData":[TD([makeQuery(id+"F13.boolean.opBoolean","COPY",FACE,{"derivedFrom":makeQuery(id+"F13.opExtrude","SWEPT_FACE",FACE,{"disambiguationData":[OSD([sQuery(id+"F12.wireOp",EDGE,"E6.right")])]})})])],"derivedFrom":makeQuery(id+"F17.opExtrude","CAP_EDGE",EDGE,{"disambiguationData":[OSD([subQ0])],"isStart":false})});}
            var Q11;
            {var subQ1=sQuery(id+"F14.wireOp",EDGE,"E8.0.9.1");Q11=makeQuery(id+"F17.boolean.opBoolean","COPY",EDGE,{"disambiguationData":[TD([makeQuery(id+"F13.boolean.opBoolean","COPY",FACE,{"derivedFrom":makeQuery(id+"F13.opExtrude","SWEPT_FACE",FACE,{"disambiguationData":[OSD([sQuery(id+"F12.wireOp",EDGE,"E6.right")])]})})])],"derivedFrom":makeQuery(id+"F17.opExtrude","CAP_EDGE",EDGE,{"disambiguationData":[OSD([subQ1])],"isStart":false})});}
            var Q12;
            {var subQ1=sQuery(id+"F14.wireOp",EDGE,"E8.0.8.0");Q12=makeQuery(id+"F17.boolean.opBoolean","COPY",EDGE,{"disambiguationData":[TD([makeQuery(id+"F13.boolean.opBoolean","COPY",FACE,{"derivedFrom":makeQuery(id+"F13.opExtrude","SWEPT_FACE",FACE,{"disambiguationData":[OSD([sQuery(id+"F12.wireOp",EDGE,"E6.right")])]})})])],"derivedFrom":makeQuery(id+"F17.opExtrude","CAP_EDGE",EDGE,{"disambiguationData":[OSD([subQ1])],"isStart":false})});}
            var Q13;
            {var subQ1=sQuery(id+"F14.wireOp",EDGE,"E8.0.8.1");Q13=makeQuery(id+"F17.boolean.opBoolean","COPY",EDGE,{"disambiguationData":[TD([makeQuery(id+"F13.boolean.opBoolean","COPY",FACE,{"derivedFrom":makeQuery(id+"F13.opExtrude","SWEPT_FACE",FACE,{"disambiguationData":[OSD([sQuery(id+"F12.wireOp",EDGE,"E6.right")])]})})])],"derivedFrom":makeQuery(id+"F17.opExtrude","CAP_EDGE",EDGE,{"disambiguationData":[OSD([subQ1])],"isStart":false})});}
            var Q14;
            {var subQ0=sQuery(id+"F14.wireOp",EDGE,"E8.0.7.0");Q14=makeQuery(id+"F17.boolean.opBoolean","COPY",EDGE,{"disambiguationData":[TD([makeQuery(id+"F13.boolean.opBoolean","COPY",FACE,{"derivedFrom":makeQuery(id+"F13.opExtrude","SWEPT_FACE",FACE,{"disambiguationData":[OSD([sQuery(id+"F12.wireOp",EDGE,"E6.right")])]})})])],"derivedFrom":makeQuery(id+"F17.opExtrude","CAP_EDGE",EDGE,{"disambiguationData":[OSD([subQ0])],"isStart":false})});}
            var Q15;
            {var subQ0=sQuery(id+"F14.wireOp",EDGE,"E8.0.7.1");Q15=makeQuery(id+"F17.boolean.opBoolean","COPY",EDGE,{"disambiguationData":[TD([makeQuery(id+"F13.boolean.opBoolean","COPY",FACE,{"derivedFrom":makeQuery(id+"F13.opExtrude","SWEPT_FACE",FACE,{"disambiguationData":[OSD([sQuery(id+"F12.wireOp",EDGE,"E6.right")])]})})])],"derivedFrom":makeQuery(id+"F17.opExtrude","CAP_EDGE",EDGE,{"disambiguationData":[OSD([subQ0])],"isStart":false})});}
            var Q16;
            {var subQ0=sQuery(id+"F14.wireOp",EDGE,"E8.0.6.0");Q16=makeQuery(id+"F17.boolean.opBoolean","COPY",EDGE,{"disambiguationData":[TD([makeQuery(id+"F13.boolean.opBoolean","COPY",FACE,{"derivedFrom":makeQuery(id+"F13.opExtrude","SWEPT_FACE",FACE,{"disambiguationData":[OSD([sQuery(id+"F12.wireOp",EDGE,"E6.right")])]})})])],"derivedFrom":makeQuery(id+"F17.opExtrude","CAP_EDGE",EDGE,{"disambiguationData":[OSD([subQ0])],"isStart":false})});}
            var Q17;
            {var subQ1=sQuery(id+"F14.wireOp",EDGE,"E8.0.6.1");Q17=makeQuery(id+"F17.boolean.opBoolean","COPY",EDGE,{"disambiguationData":[TD([makeQuery(id+"F13.boolean.opBoolean","COPY",FACE,{"derivedFrom":makeQuery(id+"F13.opExtrude","SWEPT_FACE",FACE,{"disambiguationData":[OSD([sQuery(id+"F12.wireOp",EDGE,"E6.right")])]})})])],"derivedFrom":makeQuery(id+"F17.opExtrude","CAP_EDGE",EDGE,{"disambiguationData":[OSD([subQ1])],"isStart":false})});}
            var Q18;
            {var subQ0=sQuery(id+"F14.wireOp",EDGE,"E8.0.5.0");Q18=makeQuery(id+"F17.boolean.opBoolean","COPY",EDGE,{"disambiguationData":[TD([makeQuery(id+"F13.boolean.opBoolean","COPY",FACE,{"derivedFrom":makeQuery(id+"F13.opExtrude","SWEPT_FACE",FACE,{"disambiguationData":[OSD([sQuery(id+"F12.wireOp",EDGE,"E6.right")])]})})])],"derivedFrom":makeQuery(id+"F17.opExtrude","CAP_EDGE",EDGE,{"disambiguationData":[OSD([subQ0])],"isStart":false})});}
            var Q19;
            {var subQ1=sQuery(id+"F14.wireOp",EDGE,"E8.0.5.1");Q19=makeQuery(id+"F17.boolean.opBoolean","COPY",EDGE,{"disambiguationData":[TD([makeQuery(id+"F13.boolean.opBoolean","COPY",FACE,{"derivedFrom":makeQuery(id+"F13.opExtrude","SWEPT_FACE",FACE,{"disambiguationData":[OSD([sQuery(id+"F12.wireOp",EDGE,"E6.right")])]})})])],"derivedFrom":makeQuery(id+"F17.opExtrude","CAP_EDGE",EDGE,{"disambiguationData":[OSD([subQ1])],"isStart":false})});}
            var Q20;
            {var subQ0=sQuery(id+"F14.wireOp",EDGE,"E8.0.4.0");Q20=makeQuery(id+"F17.boolean.opBoolean","COPY",EDGE,{"disambiguationData":[TD([makeQuery(id+"F13.boolean.opBoolean","COPY",FACE,{"derivedFrom":makeQuery(id+"F13.opExtrude","SWEPT_FACE",FACE,{"disambiguationData":[OSD([sQuery(id+"F12.wireOp",EDGE,"E6.right")])]})})])],"derivedFrom":makeQuery(id+"F17.opExtrude","CAP_EDGE",EDGE,{"disambiguationData":[OSD([subQ0])],"isStart":false})});}
            var Q21;
            {var subQ1=sQuery(id+"F14.wireOp",EDGE,"E8.0.4.1");Q21=makeQuery(id+"F17.boolean.opBoolean","COPY",EDGE,{"disambiguationData":[TD([makeQuery(id+"F13.boolean.opBoolean","COPY",FACE,{"derivedFrom":makeQuery(id+"F13.opExtrude","SWEPT_FACE",FACE,{"disambiguationData":[OSD([sQuery(id+"F12.wireOp",EDGE,"E6.right")])]})})])],"derivedFrom":makeQuery(id+"F17.opExtrude","CAP_EDGE",EDGE,{"disambiguationData":[OSD([subQ1])],"isStart":false})});}
            var Q22;
            {var subQ1=sQuery(id+"F14.wireOp",EDGE,"E8.0.3.0");Q22=makeQuery(id+"F17.boolean.opBoolean","COPY",EDGE,{"disambiguationData":[TD([makeQuery(id+"F13.boolean.opBoolean","COPY",FACE,{"derivedFrom":makeQuery(id+"F13.opExtrude","SWEPT_FACE",FACE,{"disambiguationData":[OSD([sQuery(id+"F12.wireOp",EDGE,"E6.right")])]})})])],"derivedFrom":makeQuery(id+"F17.opExtrude","CAP_EDGE",EDGE,{"disambiguationData":[OSD([subQ1])],"isStart":false})});}
            var Q23;
            {var subQ1=sQuery(id+"F14.wireOp",EDGE,"E8.0.3.1");Q23=makeQuery(id+"F17.boolean.opBoolean","COPY",EDGE,{"disambiguationData":[TD([makeQuery(id+"F13.boolean.opBoolean","COPY",FACE,{"derivedFrom":makeQuery(id+"F13.opExtrude","SWEPT_FACE",FACE,{"disambiguationData":[OSD([sQuery(id+"F12.wireOp",EDGE,"E6.right")])]})})])],"derivedFrom":makeQuery(id+"F17.opExtrude","CAP_EDGE",EDGE,{"disambiguationData":[OSD([subQ1])],"isStart":false})});}
            var Q24;
            {var subQ0=sQuery(id+"F14.wireOp",EDGE,"E8.0.2.0");Q24=makeQuery(id+"F17.boolean.opBoolean","COPY",EDGE,{"disambiguationData":[TD([makeQuery(id+"F13.boolean.opBoolean","COPY",FACE,{"derivedFrom":makeQuery(id+"F13.opExtrude","SWEPT_FACE",FACE,{"disambiguationData":[OSD([sQuery(id+"F12.wireOp",EDGE,"E6.right")])]})})])],"derivedFrom":makeQuery(id+"F17.opExtrude","CAP_EDGE",EDGE,{"disambiguationData":[OSD([subQ0])],"isStart":false})});}
            var Q25;
            {var subQ0=sQuery(id+"F14.wireOp",EDGE,"E8.0.2.1");Q25=makeQuery(id+"F17.boolean.opBoolean","COPY",EDGE,{"disambiguationData":[TD([makeQuery(id+"F13.boolean.opBoolean","COPY",FACE,{"derivedFrom":makeQuery(id+"F13.opExtrude","SWEPT_FACE",FACE,{"disambiguationData":[OSD([sQuery(id+"F12.wireOp",EDGE,"E6.right")])]})})])],"derivedFrom":makeQuery(id+"F17.opExtrude","CAP_EDGE",EDGE,{"disambiguationData":[OSD([subQ0])],"isStart":false})});}
            var Q26;
            {var subQ0=sQuery(id+"F14.wireOp",EDGE,"E8.0.1.0");Q26=makeQuery(id+"F17.boolean.opBoolean","COPY",EDGE,{"disambiguationData":[TD([makeQuery(id+"F13.boolean.opBoolean","COPY",FACE,{"derivedFrom":makeQuery(id+"F13.opExtrude","SWEPT_FACE",FACE,{"disambiguationData":[OSD([sQuery(id+"F12.wireOp",EDGE,"E6.right")])]})})])],"derivedFrom":makeQuery(id+"F17.opExtrude","CAP_EDGE",EDGE,{"disambiguationData":[OSD([subQ0])],"isStart":false})});}
            var Q27;
            {var subQ1=sQuery(id+"F14.wireOp",EDGE,"E8.0.1.1");Q27=makeQuery(id+"F17.boolean.opBoolean","COPY",EDGE,{"disambiguationData":[TD([makeQuery(id+"F13.boolean.opBoolean","COPY",FACE,{"derivedFrom":makeQuery(id+"F13.opExtrude","SWEPT_FACE",FACE,{"disambiguationData":[OSD([sQuery(id+"F12.wireOp",EDGE,"E6.right")])]})})])],"derivedFrom":makeQuery(id+"F17.opExtrude","CAP_EDGE",EDGE,{"disambiguationData":[OSD([subQ1])],"isStart":false})});}
            var Q28;
            {var subQ1=sQuery(id+"F14.wireOp",EDGE,"E7.top");Q28=makeQuery(id+"F17.boolean.opBoolean","COPY",EDGE,{"disambiguationData":[TD([makeQuery(id+"F13.boolean.opBoolean","COPY",FACE,{"derivedFrom":makeQuery(id+"F13.opExtrude","SWEPT_FACE",FACE,{"disambiguationData":[OSD([sQuery(id+"F12.wireOp",EDGE,"E6.right")])]})})])],"derivedFrom":makeQuery(id+"F17.opExtrude","CAP_EDGE",EDGE,{"disambiguationData":[OSD([subQ1])],"isStart":false})});}
            var Q29;
            {var subQ0=sQuery(id+"F14.wireOp",EDGE,"E7.bottom");Q29=makeQuery(id+"F17.boolean.opBoolean","COPY",EDGE,{"disambiguationData":[TD([makeQuery(id+"F13.boolean.opBoolean","COPY",FACE,{"derivedFrom":makeQuery(id+"F13.opExtrude","SWEPT_FACE",FACE,{"disambiguationData":[OSD([sQuery(id+"F12.wireOp",EDGE,"E6.right")])]})})])],"derivedFrom":makeQuery(id+"F17.opExtrude","CAP_EDGE",EDGE,{"disambiguationData":[OSD([subQ0])],"isStart":false})});}
            var Q30;
            {var subQ1=sQuery(id+"F14.wireOp",EDGE,"E7.top");Q30=makeQuery(id+"F17.boolean.opBoolean","COPY",EDGE,{"disambiguationData":[TD([makeQuery(id+"F13.boolean.opBoolean","COPY",FACE,{"derivedFrom":makeQuery(id+"F13.opExtrude","SWEPT_FACE",FACE,{"disambiguationData":[OSD([sQuery(id+"F12.wireOp",EDGE,"E6.left")])]})})])],"derivedFrom":makeQuery(id+"F17.opExtrude","CAP_EDGE",EDGE,{"disambiguationData":[OSD([subQ1])],"isStart":false})});}
            var Q31;
            {var subQ1=sQuery(id+"F14.wireOp",EDGE,"E7.bottom");Q31=makeQuery(id+"F17.boolean.opBoolean","COPY",EDGE,{"disambiguationData":[TD([makeQuery(id+"F13.boolean.opBoolean","COPY",FACE,{"derivedFrom":makeQuery(id+"F13.opExtrude","SWEPT_FACE",FACE,{"disambiguationData":[OSD([sQuery(id+"F12.wireOp",EDGE,"E6.left")])]})})])],"derivedFrom":makeQuery(id+"F17.opExtrude","CAP_EDGE",EDGE,{"disambiguationData":[OSD([subQ1])],"isStart":false})});}
            var Q32;
            {var subQ0=sQuery(id+"F14.wireOp",EDGE,"E8.0.1.0");Q32=makeQuery(id+"F17.boolean.opBoolean","COPY",EDGE,{"disambiguationData":[TD([makeQuery(id+"F13.boolean.opBoolean","COPY",FACE,{"derivedFrom":makeQuery(id+"F13.opExtrude","SWEPT_FACE",FACE,{"disambiguationData":[OSD([sQuery(id+"F12.wireOp",EDGE,"E6.left")])]})})])],"derivedFrom":makeQuery(id+"F17.opExtrude","CAP_EDGE",EDGE,{"disambiguationData":[OSD([subQ0])],"isStart":false})});}
            var Q33;
            {var subQ0=sQuery(id+"F14.wireOp",EDGE,"E8.0.1.1");Q33=makeQuery(id+"F17.boolean.opBoolean","COPY",EDGE,{"disambiguationData":[TD([makeQuery(id+"F13.boolean.opBoolean","COPY",FACE,{"derivedFrom":makeQuery(id+"F13.opExtrude","SWEPT_FACE",FACE,{"disambiguationData":[OSD([sQuery(id+"F12.wireOp",EDGE,"E6.left")])]})})])],"derivedFrom":makeQuery(id+"F17.opExtrude","CAP_EDGE",EDGE,{"disambiguationData":[OSD([subQ0])],"isStart":false})});}
            var Q34;
            {var subQ1=sQuery(id+"F14.wireOp",EDGE,"E8.0.2.0");Q34=makeQuery(id+"F17.boolean.opBoolean","COPY",EDGE,{"disambiguationData":[TD([makeQuery(id+"F13.boolean.opBoolean","COPY",FACE,{"derivedFrom":makeQuery(id+"F13.opExtrude","SWEPT_FACE",FACE,{"disambiguationData":[OSD([sQuery(id+"F12.wireOp",EDGE,"E6.left")])]})})])],"derivedFrom":makeQuery(id+"F17.opExtrude","CAP_EDGE",EDGE,{"disambiguationData":[OSD([subQ1])],"isStart":false})});}
            var Q35;
            {var subQ1=sQuery(id+"F14.wireOp",EDGE,"E8.0.2.1");Q35=makeQuery(id+"F17.boolean.opBoolean","COPY",EDGE,{"disambiguationData":[TD([makeQuery(id+"F13.boolean.opBoolean","COPY",FACE,{"derivedFrom":makeQuery(id+"F13.opExtrude","SWEPT_FACE",FACE,{"disambiguationData":[OSD([sQuery(id+"F12.wireOp",EDGE,"E6.left")])]})})])],"derivedFrom":makeQuery(id+"F17.opExtrude","CAP_EDGE",EDGE,{"disambiguationData":[OSD([subQ1])],"isStart":false})});}
            var Q36;
            {var subQ0=sQuery(id+"F14.wireOp",EDGE,"E8.0.3.0");Q36=makeQuery(id+"F17.boolean.opBoolean","COPY",EDGE,{"disambiguationData":[TD([makeQuery(id+"F13.boolean.opBoolean","COPY",FACE,{"derivedFrom":makeQuery(id+"F13.opExtrude","SWEPT_FACE",FACE,{"disambiguationData":[OSD([sQuery(id+"F12.wireOp",EDGE,"E6.left")])]})})])],"derivedFrom":makeQuery(id+"F17.opExtrude","CAP_EDGE",EDGE,{"disambiguationData":[OSD([subQ0])],"isStart":false})});}
            var Q37;
            {var subQ1=sQuery(id+"F14.wireOp",EDGE,"E8.0.3.1");Q37=makeQuery(id+"F17.boolean.opBoolean","COPY",EDGE,{"disambiguationData":[TD([makeQuery(id+"F13.boolean.opBoolean","COPY",FACE,{"derivedFrom":makeQuery(id+"F13.opExtrude","SWEPT_FACE",FACE,{"disambiguationData":[OSD([sQuery(id+"F12.wireOp",EDGE,"E6.left")])]})})])],"derivedFrom":makeQuery(id+"F17.opExtrude","CAP_EDGE",EDGE,{"disambiguationData":[OSD([subQ1])],"isStart":false})});}
            var Q38;
            {var subQ0=sQuery(id+"F14.wireOp",EDGE,"E8.0.4.0");Q38=makeQuery(id+"F17.boolean.opBoolean","COPY",EDGE,{"disambiguationData":[TD([makeQuery(id+"F13.boolean.opBoolean","COPY",FACE,{"derivedFrom":makeQuery(id+"F13.opExtrude","SWEPT_FACE",FACE,{"disambiguationData":[OSD([sQuery(id+"F12.wireOp",EDGE,"E6.left")])]})})])],"derivedFrom":makeQuery(id+"F17.opExtrude","CAP_EDGE",EDGE,{"disambiguationData":[OSD([subQ0])],"isStart":false})});}
            var Q39;
            {var subQ1=sQuery(id+"F14.wireOp",EDGE,"E8.0.4.1");Q39=makeQuery(id+"F17.boolean.opBoolean","COPY",EDGE,{"disambiguationData":[TD([makeQuery(id+"F13.boolean.opBoolean","COPY",FACE,{"derivedFrom":makeQuery(id+"F13.opExtrude","SWEPT_FACE",FACE,{"disambiguationData":[OSD([sQuery(id+"F12.wireOp",EDGE,"E6.left")])]})})])],"derivedFrom":makeQuery(id+"F17.opExtrude","CAP_EDGE",EDGE,{"disambiguationData":[OSD([subQ1])],"isStart":false})});}
            var Q40;
            {var subQ1=sQuery(id+"F14.wireOp",EDGE,"E8.0.5.0");Q40=makeQuery(id+"F17.boolean.opBoolean","COPY",EDGE,{"disambiguationData":[TD([makeQuery(id+"F13.boolean.opBoolean","COPY",FACE,{"derivedFrom":makeQuery(id+"F13.opExtrude","SWEPT_FACE",FACE,{"disambiguationData":[OSD([sQuery(id+"F12.wireOp",EDGE,"E6.left")])]})})])],"derivedFrom":makeQuery(id+"F17.opExtrude","CAP_EDGE",EDGE,{"disambiguationData":[OSD([subQ1])],"isStart":false})});}
            var Q41;
            {var subQ1=sQuery(id+"F14.wireOp",EDGE,"E8.0.5.1");Q41=makeQuery(id+"F17.boolean.opBoolean","COPY",EDGE,{"disambiguationData":[TD([makeQuery(id+"F13.boolean.opBoolean","COPY",FACE,{"derivedFrom":makeQuery(id+"F13.opExtrude","SWEPT_FACE",FACE,{"disambiguationData":[OSD([sQuery(id+"F12.wireOp",EDGE,"E6.left")])]})})])],"derivedFrom":makeQuery(id+"F17.opExtrude","CAP_EDGE",EDGE,{"disambiguationData":[OSD([subQ1])],"isStart":false})});}
            var Q42;
            {var subQ0=sQuery(id+"F14.wireOp",EDGE,"E8.0.6.0");Q42=makeQuery(id+"F17.boolean.opBoolean","COPY",EDGE,{"disambiguationData":[TD([makeQuery(id+"F13.boolean.opBoolean","COPY",FACE,{"derivedFrom":makeQuery(id+"F13.opExtrude","SWEPT_FACE",FACE,{"disambiguationData":[OSD([sQuery(id+"F12.wireOp",EDGE,"E6.left")])]})})])],"derivedFrom":makeQuery(id+"F17.opExtrude","CAP_EDGE",EDGE,{"disambiguationData":[OSD([subQ0])],"isStart":false})});}
            var Q43;
            {var subQ0=sQuery(id+"F14.wireOp",EDGE,"E8.0.6.1");Q43=makeQuery(id+"F17.boolean.opBoolean","COPY",EDGE,{"disambiguationData":[TD([makeQuery(id+"F13.boolean.opBoolean","COPY",FACE,{"derivedFrom":makeQuery(id+"F13.opExtrude","SWEPT_FACE",FACE,{"disambiguationData":[OSD([sQuery(id+"F12.wireOp",EDGE,"E6.left")])]})})])],"derivedFrom":makeQuery(id+"F17.opExtrude","CAP_EDGE",EDGE,{"disambiguationData":[OSD([subQ0])],"isStart":false})});}
            var Q44;
            {var subQ1=sQuery(id+"F14.wireOp",EDGE,"E8.0.7.0");Q44=makeQuery(id+"F17.boolean.opBoolean","COPY",EDGE,{"disambiguationData":[TD([makeQuery(id+"F13.boolean.opBoolean","COPY",FACE,{"derivedFrom":makeQuery(id+"F13.opExtrude","SWEPT_FACE",FACE,{"disambiguationData":[OSD([sQuery(id+"F12.wireOp",EDGE,"E6.left")])]})})])],"derivedFrom":makeQuery(id+"F17.opExtrude","CAP_EDGE",EDGE,{"disambiguationData":[OSD([subQ1])],"isStart":false})});}
            var Q45;
            {var subQ1=sQuery(id+"F14.wireOp",EDGE,"E8.0.7.1");Q45=makeQuery(id+"F17.boolean.opBoolean","COPY",EDGE,{"disambiguationData":[TD([makeQuery(id+"F13.boolean.opBoolean","COPY",FACE,{"derivedFrom":makeQuery(id+"F13.opExtrude","SWEPT_FACE",FACE,{"disambiguationData":[OSD([sQuery(id+"F12.wireOp",EDGE,"E6.left")])]})})])],"derivedFrom":makeQuery(id+"F17.opExtrude","CAP_EDGE",EDGE,{"disambiguationData":[OSD([subQ1])],"isStart":false})});}
            var Q46;
            {var subQ0=sQuery(id+"F14.wireOp",EDGE,"E8.0.8.0");Q46=makeQuery(id+"F17.boolean.opBoolean","COPY",EDGE,{"disambiguationData":[TD([makeQuery(id+"F13.boolean.opBoolean","COPY",FACE,{"derivedFrom":makeQuery(id+"F13.opExtrude","SWEPT_FACE",FACE,{"disambiguationData":[OSD([sQuery(id+"F12.wireOp",EDGE,"E6.left")])]})})])],"derivedFrom":makeQuery(id+"F17.opExtrude","CAP_EDGE",EDGE,{"disambiguationData":[OSD([subQ0])],"isStart":false})});}
            var Q47;
            {var subQ1=sQuery(id+"F14.wireOp",EDGE,"E8.0.8.1");Q47=makeQuery(id+"F17.boolean.opBoolean","COPY",EDGE,{"disambiguationData":[TD([makeQuery(id+"F13.boolean.opBoolean","COPY",FACE,{"derivedFrom":makeQuery(id+"F13.opExtrude","SWEPT_FACE",FACE,{"disambiguationData":[OSD([sQuery(id+"F12.wireOp",EDGE,"E6.left")])]})})])],"derivedFrom":makeQuery(id+"F17.opExtrude","CAP_EDGE",EDGE,{"disambiguationData":[OSD([subQ1])],"isStart":false})});}
            var Q48;
            {var subQ0=sQuery(id+"F14.wireOp",EDGE,"E8.0.9.0");Q48=makeQuery(id+"F17.boolean.opBoolean","COPY",EDGE,{"disambiguationData":[TD([makeQuery(id+"F13.boolean.opBoolean","COPY",FACE,{"derivedFrom":makeQuery(id+"F13.opExtrude","SWEPT_FACE",FACE,{"disambiguationData":[OSD([sQuery(id+"F12.wireOp",EDGE,"E6.left")])]})})])],"derivedFrom":makeQuery(id+"F17.opExtrude","CAP_EDGE",EDGE,{"disambiguationData":[OSD([subQ0])],"isStart":false})});}
            var Q49;
            {var subQ1=sQuery(id+"F14.wireOp",EDGE,"E8.0.9.1");Q49=makeQuery(id+"F17.boolean.opBoolean","COPY",EDGE,{"disambiguationData":[TD([makeQuery(id+"F13.boolean.opBoolean","COPY",FACE,{"derivedFrom":makeQuery(id+"F13.opExtrude","SWEPT_FACE",FACE,{"disambiguationData":[OSD([sQuery(id+"F12.wireOp",EDGE,"E6.left")])]})})])],"derivedFrom":makeQuery(id+"F17.opExtrude","CAP_EDGE",EDGE,{"disambiguationData":[OSD([subQ1])],"isStart":false})});}
            var Q50;
            {var subQ1=sQuery(id+"F14.wireOp",EDGE,"E8.0.10.0");Q50=makeQuery(id+"F17.boolean.opBoolean","COPY",EDGE,{"disambiguationData":[TD([makeQuery(id+"F13.boolean.opBoolean","COPY",FACE,{"derivedFrom":makeQuery(id+"F13.opExtrude","SWEPT_FACE",FACE,{"disambiguationData":[OSD([sQuery(id+"F12.wireOp",EDGE,"E6.left")])]})})])],"derivedFrom":makeQuery(id+"F17.opExtrude","CAP_EDGE",EDGE,{"disambiguationData":[OSD([subQ1])],"isStart":false})});}
            var Q51;
            {var subQ1=sQuery(id+"F14.wireOp",EDGE,"E8.0.10.1");Q51=makeQuery(id+"F17.boolean.opBoolean","COPY",EDGE,{"disambiguationData":[TD([makeQuery(id+"F13.boolean.opBoolean","COPY",FACE,{"derivedFrom":makeQuery(id+"F13.opExtrude","SWEPT_FACE",FACE,{"disambiguationData":[OSD([sQuery(id+"F12.wireOp",EDGE,"E6.left")])]})})])],"derivedFrom":makeQuery(id+"F17.opExtrude","CAP_EDGE",EDGE,{"disambiguationData":[OSD([subQ1])],"isStart":false})});}
            var Q52;
            {var subQ0=sQuery(id+"F14.wireOp",EDGE,"E8.0.11.0");Q52=makeQuery(id+"F17.boolean.opBoolean","COPY",EDGE,{"disambiguationData":[TD([makeQuery(id+"F13.boolean.opBoolean","COPY",FACE,{"derivedFrom":makeQuery(id+"F13.opExtrude","SWEPT_FACE",FACE,{"disambiguationData":[OSD([sQuery(id+"F12.wireOp",EDGE,"E6.left")])]})})])],"derivedFrom":makeQuery(id+"F17.opExtrude","CAP_EDGE",EDGE,{"disambiguationData":[OSD([subQ0])],"isStart":false})});}
            var Q53;
            {var subQ0=sQuery(id+"F14.wireOp",EDGE,"E8.0.11.1");Q53=makeQuery(id+"F17.boolean.opBoolean","COPY",EDGE,{"disambiguationData":[TD([makeQuery(id+"F13.boolean.opBoolean","COPY",FACE,{"derivedFrom":makeQuery(id+"F13.opExtrude","SWEPT_FACE",FACE,{"disambiguationData":[OSD([sQuery(id+"F12.wireOp",EDGE,"E6.left")])]})})])],"derivedFrom":makeQuery(id+"F17.opExtrude","CAP_EDGE",EDGE,{"disambiguationData":[OSD([subQ0])],"isStart":false})});}
            var Q54;
            {var subQ1=sQuery(id+"F14.wireOp",EDGE,"E8.0.12.0");Q54=makeQuery(id+"F17.boolean.opBoolean","COPY",EDGE,{"disambiguationData":[TD([makeQuery(id+"F13.boolean.opBoolean","COPY",FACE,{"derivedFrom":makeQuery(id+"F13.opExtrude","SWEPT_FACE",FACE,{"disambiguationData":[OSD([sQuery(id+"F12.wireOp",EDGE,"E6.left")])]})})])],"derivedFrom":makeQuery(id+"F17.opExtrude","CAP_EDGE",EDGE,{"disambiguationData":[OSD([subQ1])],"isStart":false})});}
            var Q55;
            {var subQ1=sQuery(id+"F14.wireOp",EDGE,"E8.0.12.1");Q55=makeQuery(id+"F17.boolean.opBoolean","COPY",EDGE,{"disambiguationData":[TD([makeQuery(id+"F13.boolean.opBoolean","COPY",FACE,{"derivedFrom":makeQuery(id+"F13.opExtrude","SWEPT_FACE",FACE,{"disambiguationData":[OSD([sQuery(id+"F12.wireOp",EDGE,"E6.left")])]})})])],"derivedFrom":makeQuery(id+"F17.opExtrude","CAP_EDGE",EDGE,{"disambiguationData":[OSD([subQ1])],"isStart":false})});}
            var Q56;
            {var subQ0=sQuery(id+"F14.wireOp",EDGE,"E8.0.13.0");Q56=makeQuery(id+"F17.boolean.opBoolean","COPY",EDGE,{"disambiguationData":[TD([makeQuery(id+"F13.boolean.opBoolean","COPY",FACE,{"derivedFrom":makeQuery(id+"F13.opExtrude","SWEPT_FACE",FACE,{"disambiguationData":[OSD([sQuery(id+"F12.wireOp",EDGE,"E6.left")])]})})])],"derivedFrom":makeQuery(id+"F17.opExtrude","CAP_EDGE",EDGE,{"disambiguationData":[OSD([subQ0])],"isStart":false})});}
            var Q57;
            {var subQ1=sQuery(id+"F14.wireOp",EDGE,"E8.0.13.1");Q57=makeQuery(id+"F17.boolean.opBoolean","COPY",EDGE,{"disambiguationData":[TD([makeQuery(id+"F13.boolean.opBoolean","COPY",FACE,{"derivedFrom":makeQuery(id+"F13.opExtrude","SWEPT_FACE",FACE,{"disambiguationData":[OSD([sQuery(id+"F12.wireOp",EDGE,"E6.left")])]})})])],"derivedFrom":makeQuery(id+"F17.opExtrude","CAP_EDGE",EDGE,{"disambiguationData":[OSD([subQ1])],"isStart":false})});}
            var Q58;
            {var subQ0=sQuery(id+"F14.wireOp",EDGE,"E8.0.14.0");Q58=makeQuery(id+"F17.boolean.opBoolean","COPY",EDGE,{"disambiguationData":[TD([makeQuery(id+"F13.boolean.opBoolean","COPY",FACE,{"derivedFrom":makeQuery(id+"F13.opExtrude","SWEPT_FACE",FACE,{"disambiguationData":[OSD([sQuery(id+"F12.wireOp",EDGE,"E6.left")])]})})])],"derivedFrom":makeQuery(id+"F17.opExtrude","CAP_EDGE",EDGE,{"disambiguationData":[OSD([subQ0])],"isStart":false})});}
            var Q59;
            {var subQ1=sQuery(id+"F14.wireOp",EDGE,"E8.0.14.1");Q59=makeQuery(id+"F17.boolean.opBoolean","COPY",EDGE,{"disambiguationData":[TD([makeQuery(id+"F13.boolean.opBoolean","COPY",FACE,{"derivedFrom":makeQuery(id+"F13.opExtrude","SWEPT_FACE",FACE,{"disambiguationData":[OSD([sQuery(id+"F12.wireOp",EDGE,"E6.left")])]})})])],"derivedFrom":makeQuery(id+"F17.opExtrude","CAP_EDGE",EDGE,{"disambiguationData":[OSD([subQ1])],"isStart":false})});}
            var Q60;
            {var subQ0=sQuery(id+"F14.wireOp",EDGE,"E11.0.14.1");Q60=makeQuery(id+"F17.boolean.opBoolean","COPY",EDGE,{"derivedFrom":makeQuery(id+"F17.opExtrude","CAP_EDGE",EDGE,{"disambiguationData":[OSD([subQ0]),TDD([makeQuery(id+"F14.imprint","IMPRINT",EDGE,{"disambiguationData":[TD([[makeQuery(id+"F14.imprint","INTERSECT",VERTEX,{"derivedFrom":[subQ0,sQuery(id+"F14.wireOp",EDGE,"E11.0.14.3")]}),1.0]])],"derivedFrom":subQ0})])],"isStart":false})});}
            var Q61;
            {var subQ0=sQuery(id+"F14.wireOp",EDGE,"E11.0.14.0");Q61=makeQuery(id+"F17.boolean.opBoolean","COPY",EDGE,{"derivedFrom":makeQuery(id+"F17.opExtrude","CAP_EDGE",EDGE,{"disambiguationData":[OSD([subQ0]),TDD([makeQuery(id+"F14.imprint","IMPRINT",EDGE,{"disambiguationData":[TD([[makeQuery(id+"F14.imprint","INTERSECT",VERTEX,{"derivedFrom":[subQ0,sQuery(id+"F14.wireOp",EDGE,"E11.0.14.3")]}),1.0]])],"derivedFrom":subQ0})])],"isStart":false})});}
            var Q62;
            {var subQ0=sQuery(id+"F14.wireOp",EDGE,"E11.0.13.0");Q62=makeQuery(id+"F17.boolean.opBoolean","COPY",EDGE,{"derivedFrom":makeQuery(id+"F17.opExtrude","CAP_EDGE",EDGE,{"disambiguationData":[OSD([subQ0]),TDD([makeQuery(id+"F14.imprint","IMPRINT",EDGE,{"disambiguationData":[TD([[makeQuery(id+"F14.imprint","INTERSECT",VERTEX,{"derivedFrom":[subQ0,sQuery(id+"F14.wireOp",EDGE,"E11.0.13.3")]}),1.0]])],"derivedFrom":subQ0})])],"isStart":false})});}
            var Q63;
            {var subQ0=sQuery(id+"F14.wireOp",EDGE,"E11.0.13.1");Q63=makeQuery(id+"F17.boolean.opBoolean","COPY",EDGE,{"derivedFrom":makeQuery(id+"F17.opExtrude","CAP_EDGE",EDGE,{"disambiguationData":[OSD([subQ0]),TDD([makeQuery(id+"F14.imprint","IMPRINT",EDGE,{"disambiguationData":[TD([[makeQuery(id+"F14.imprint","INTERSECT",VERTEX,{"derivedFrom":[subQ0,sQuery(id+"F14.wireOp",EDGE,"E11.0.13.3")]}),1.0]])],"derivedFrom":subQ0})])],"isStart":false})});}
            var Q64;
            {var subQ0=sQuery(id+"F14.wireOp",EDGE,"E11.0.12.0");Q64=makeQuery(id+"F17.boolean.opBoolean","COPY",EDGE,{"derivedFrom":makeQuery(id+"F17.opExtrude","CAP_EDGE",EDGE,{"disambiguationData":[OSD([subQ0]),TDD([makeQuery(id+"F14.imprint","IMPRINT",EDGE,{"disambiguationData":[TD([[makeQuery(id+"F14.imprint","INTERSECT",VERTEX,{"derivedFrom":[subQ0,sQuery(id+"F14.wireOp",EDGE,"E11.0.12.3")]}),1.0]])],"derivedFrom":subQ0})])],"isStart":false})});}
            var Q65;
            {var subQ0=sQuery(id+"F14.wireOp",EDGE,"E11.0.12.1");Q65=makeQuery(id+"F17.boolean.opBoolean","COPY",EDGE,{"derivedFrom":makeQuery(id+"F17.opExtrude","CAP_EDGE",EDGE,{"disambiguationData":[OSD([subQ0]),TDD([makeQuery(id+"F14.imprint","IMPRINT",EDGE,{"disambiguationData":[TD([[makeQuery(id+"F14.imprint","INTERSECT",VERTEX,{"derivedFrom":[subQ0,sQuery(id+"F14.wireOp",EDGE,"E11.0.12.3")]}),1.0]])],"derivedFrom":subQ0})])],"isStart":false})});}
            var Q66;
            {var subQ0=sQuery(id+"F14.wireOp",EDGE,"E11.0.11.0");Q66=makeQuery(id+"F17.boolean.opBoolean","COPY",EDGE,{"derivedFrom":makeQuery(id+"F17.opExtrude","CAP_EDGE",EDGE,{"disambiguationData":[OSD([subQ0]),TDD([makeQuery(id+"F14.imprint","IMPRINT",EDGE,{"disambiguationData":[TD([[makeQuery(id+"F14.imprint","INTERSECT",VERTEX,{"derivedFrom":[subQ0,sQuery(id+"F14.wireOp",EDGE,"E11.0.11.3")]}),1.0]])],"derivedFrom":subQ0})])],"isStart":false})});}
            var Q67;
            {var subQ0=sQuery(id+"F14.wireOp",EDGE,"E11.0.11.1");Q67=makeQuery(id+"F17.boolean.opBoolean","COPY",EDGE,{"derivedFrom":makeQuery(id+"F17.opExtrude","CAP_EDGE",EDGE,{"disambiguationData":[OSD([subQ0]),TDD([makeQuery(id+"F14.imprint","IMPRINT",EDGE,{"disambiguationData":[TD([[makeQuery(id+"F14.imprint","INTERSECT",VERTEX,{"derivedFrom":[subQ0,sQuery(id+"F14.wireOp",EDGE,"E11.0.11.3")]}),1.0]])],"derivedFrom":subQ0})])],"isStart":false})});}
            var Q68;
            {var subQ0=sQuery(id+"F14.wireOp",EDGE,"E11.0.10.0");Q68=makeQuery(id+"F17.boolean.opBoolean","COPY",EDGE,{"derivedFrom":makeQuery(id+"F17.opExtrude","CAP_EDGE",EDGE,{"disambiguationData":[OSD([subQ0]),TDD([makeQuery(id+"F14.imprint","IMPRINT",EDGE,{"disambiguationData":[TD([[makeQuery(id+"F14.imprint","INTERSECT",VERTEX,{"derivedFrom":[subQ0,sQuery(id+"F14.wireOp",EDGE,"E11.0.10.3")]}),1.0]])],"derivedFrom":subQ0})])],"isStart":false})});}
            var Q69;
            {var subQ0=sQuery(id+"F14.wireOp",EDGE,"E11.0.10.1");Q69=makeQuery(id+"F17.boolean.opBoolean","COPY",EDGE,{"derivedFrom":makeQuery(id+"F17.opExtrude","CAP_EDGE",EDGE,{"disambiguationData":[OSD([subQ0]),TDD([makeQuery(id+"F14.imprint","IMPRINT",EDGE,{"disambiguationData":[TD([[makeQuery(id+"F14.imprint","INTERSECT",VERTEX,{"derivedFrom":[subQ0,sQuery(id+"F14.wireOp",EDGE,"E11.0.10.3")]}),1.0]])],"derivedFrom":subQ0})])],"isStart":false})});}
            var Q70;
            {var subQ0=sQuery(id+"F14.wireOp",EDGE,"E11.0.9.0");Q70=makeQuery(id+"F17.boolean.opBoolean","COPY",EDGE,{"derivedFrom":makeQuery(id+"F17.opExtrude","CAP_EDGE",EDGE,{"disambiguationData":[OSD([subQ0]),TDD([makeQuery(id+"F14.imprint","IMPRINT",EDGE,{"disambiguationData":[TD([[makeQuery(id+"F14.imprint","INTERSECT",VERTEX,{"derivedFrom":[subQ0,sQuery(id+"F14.wireOp",EDGE,"E11.0.9.3")]}),1.0]])],"derivedFrom":subQ0})])],"isStart":false})});}
            var Q71;
            {var subQ0=sQuery(id+"F14.wireOp",EDGE,"E11.0.9.1");Q71=makeQuery(id+"F17.boolean.opBoolean","COPY",EDGE,{"derivedFrom":makeQuery(id+"F17.opExtrude","CAP_EDGE",EDGE,{"disambiguationData":[OSD([subQ0]),TDD([makeQuery(id+"F14.imprint","IMPRINT",EDGE,{"disambiguationData":[TD([[makeQuery(id+"F14.imprint","INTERSECT",VERTEX,{"derivedFrom":[subQ0,sQuery(id+"F14.wireOp",EDGE,"E11.0.9.3")]}),1.0]])],"derivedFrom":subQ0})])],"isStart":false})});}
            var Q72;
            {var subQ0=sQuery(id+"F14.wireOp",EDGE,"E11.0.8.0");Q72=makeQuery(id+"F17.boolean.opBoolean","COPY",EDGE,{"derivedFrom":makeQuery(id+"F17.opExtrude","CAP_EDGE",EDGE,{"disambiguationData":[OSD([subQ0]),TDD([makeQuery(id+"F14.imprint","IMPRINT",EDGE,{"disambiguationData":[TD([[makeQuery(id+"F14.imprint","INTERSECT",VERTEX,{"derivedFrom":[subQ0,sQuery(id+"F14.wireOp",EDGE,"E11.0.8.3")]}),1.0]])],"derivedFrom":subQ0})])],"isStart":false})});}
            var Q73;
            {var subQ0=sQuery(id+"F14.wireOp",EDGE,"E11.0.8.1");Q73=makeQuery(id+"F17.boolean.opBoolean","COPY",EDGE,{"derivedFrom":makeQuery(id+"F17.opExtrude","CAP_EDGE",EDGE,{"disambiguationData":[OSD([subQ0]),TDD([makeQuery(id+"F14.imprint","IMPRINT",EDGE,{"disambiguationData":[TD([[makeQuery(id+"F14.imprint","INTERSECT",VERTEX,{"derivedFrom":[subQ0,sQuery(id+"F14.wireOp",EDGE,"E11.0.8.3")]}),1.0]])],"derivedFrom":subQ0})])],"isStart":false})});}
            var Q74;
            {var subQ0=sQuery(id+"F14.wireOp",EDGE,"E11.0.7.0");Q74=makeQuery(id+"F17.boolean.opBoolean","COPY",EDGE,{"derivedFrom":makeQuery(id+"F17.opExtrude","CAP_EDGE",EDGE,{"disambiguationData":[OSD([subQ0]),TDD([makeQuery(id+"F14.imprint","IMPRINT",EDGE,{"disambiguationData":[TD([[makeQuery(id+"F14.imprint","INTERSECT",VERTEX,{"derivedFrom":[subQ0,sQuery(id+"F14.wireOp",EDGE,"E11.0.7.3")]}),1.0]])],"derivedFrom":subQ0})])],"isStart":false})});}
            var Q75;
            {var subQ0=sQuery(id+"F14.wireOp",EDGE,"E11.0.7.1");Q75=makeQuery(id+"F17.boolean.opBoolean","COPY",EDGE,{"derivedFrom":makeQuery(id+"F17.opExtrude","CAP_EDGE",EDGE,{"disambiguationData":[OSD([subQ0]),TDD([makeQuery(id+"F14.imprint","IMPRINT",EDGE,{"disambiguationData":[TD([[makeQuery(id+"F14.imprint","INTERSECT",VERTEX,{"derivedFrom":[subQ0,sQuery(id+"F14.wireOp",EDGE,"E11.0.7.3")]}),1.0]])],"derivedFrom":subQ0})])],"isStart":false})});}
            var Q76;
            {var subQ0=sQuery(id+"F14.wireOp",EDGE,"E11.0.6.0");Q76=makeQuery(id+"F17.boolean.opBoolean","COPY",EDGE,{"derivedFrom":makeQuery(id+"F17.opExtrude","CAP_EDGE",EDGE,{"disambiguationData":[OSD([subQ0]),TDD([makeQuery(id+"F14.imprint","IMPRINT",EDGE,{"disambiguationData":[TD([[makeQuery(id+"F14.imprint","INTERSECT",VERTEX,{"derivedFrom":[subQ0,sQuery(id+"F14.wireOp",EDGE,"E11.0.6.3")]}),1.0]])],"derivedFrom":subQ0})])],"isStart":false})});}
            var Q77;
            {var subQ0=sQuery(id+"F14.wireOp",EDGE,"E11.0.6.1");Q77=makeQuery(id+"F17.boolean.opBoolean","COPY",EDGE,{"derivedFrom":makeQuery(id+"F17.opExtrude","CAP_EDGE",EDGE,{"disambiguationData":[OSD([subQ0]),TDD([makeQuery(id+"F14.imprint","IMPRINT",EDGE,{"disambiguationData":[TD([[makeQuery(id+"F14.imprint","INTERSECT",VERTEX,{"derivedFrom":[subQ0,sQuery(id+"F14.wireOp",EDGE,"E11.0.6.3")]}),1.0]])],"derivedFrom":subQ0})])],"isStart":false})});}
            var Q78;
            {var subQ0=sQuery(id+"F14.wireOp",EDGE,"E11.0.5.0");Q78=makeQuery(id+"F17.boolean.opBoolean","COPY",EDGE,{"derivedFrom":makeQuery(id+"F17.opExtrude","CAP_EDGE",EDGE,{"disambiguationData":[OSD([subQ0]),TDD([makeQuery(id+"F14.imprint","IMPRINT",EDGE,{"disambiguationData":[TD([[makeQuery(id+"F14.imprint","INTERSECT",VERTEX,{"derivedFrom":[subQ0,sQuery(id+"F14.wireOp",EDGE,"E11.0.5.3")]}),1.0]])],"derivedFrom":subQ0})])],"isStart":false})});}
            var Q79;
            {var subQ0=sQuery(id+"F14.wireOp",EDGE,"E11.0.5.1");Q79=makeQuery(id+"F17.boolean.opBoolean","COPY",EDGE,{"derivedFrom":makeQuery(id+"F17.opExtrude","CAP_EDGE",EDGE,{"disambiguationData":[OSD([subQ0]),TDD([makeQuery(id+"F14.imprint","IMPRINT",EDGE,{"disambiguationData":[TD([[makeQuery(id+"F14.imprint","INTERSECT",VERTEX,{"derivedFrom":[subQ0,sQuery(id+"F14.wireOp",EDGE,"E11.0.5.3")]}),1.0]])],"derivedFrom":subQ0})])],"isStart":false})});}
            var Q80;
            {var subQ0=sQuery(id+"F14.wireOp",EDGE,"E11.0.4.0");Q80=makeQuery(id+"F17.boolean.opBoolean","COPY",EDGE,{"derivedFrom":makeQuery(id+"F17.opExtrude","CAP_EDGE",EDGE,{"disambiguationData":[OSD([subQ0]),TDD([makeQuery(id+"F14.imprint","IMPRINT",EDGE,{"disambiguationData":[TD([[makeQuery(id+"F14.imprint","INTERSECT",VERTEX,{"derivedFrom":[subQ0,sQuery(id+"F14.wireOp",EDGE,"E11.0.4.3")]}),1.0]])],"derivedFrom":subQ0})])],"isStart":false})});}
            var Q81;
            {var subQ0=sQuery(id+"F14.wireOp",EDGE,"E11.0.4.1");Q81=makeQuery(id+"F17.boolean.opBoolean","COPY",EDGE,{"derivedFrom":makeQuery(id+"F17.opExtrude","CAP_EDGE",EDGE,{"disambiguationData":[OSD([subQ0]),TDD([makeQuery(id+"F14.imprint","IMPRINT",EDGE,{"disambiguationData":[TD([[makeQuery(id+"F14.imprint","INTERSECT",VERTEX,{"derivedFrom":[subQ0,sQuery(id+"F14.wireOp",EDGE,"E11.0.4.3")]}),1.0]])],"derivedFrom":subQ0})])],"isStart":false})});}
            var Q82;
            {var subQ0=sQuery(id+"F14.wireOp",EDGE,"E11.0.3.0");Q82=makeQuery(id+"F17.boolean.opBoolean","COPY",EDGE,{"derivedFrom":makeQuery(id+"F17.opExtrude","CAP_EDGE",EDGE,{"disambiguationData":[OSD([subQ0]),TDD([makeQuery(id+"F14.imprint","IMPRINT",EDGE,{"disambiguationData":[TD([[makeQuery(id+"F14.imprint","INTERSECT",VERTEX,{"derivedFrom":[subQ0,sQuery(id+"F14.wireOp",EDGE,"E11.0.3.3")]}),1.0]])],"derivedFrom":subQ0})])],"isStart":false})});}
            var Q83;
            {var subQ0=sQuery(id+"F14.wireOp",EDGE,"E11.0.3.1");Q83=makeQuery(id+"F17.boolean.opBoolean","COPY",EDGE,{"derivedFrom":makeQuery(id+"F17.opExtrude","CAP_EDGE",EDGE,{"disambiguationData":[OSD([subQ0]),TDD([makeQuery(id+"F14.imprint","IMPRINT",EDGE,{"disambiguationData":[TD([[makeQuery(id+"F14.imprint","INTERSECT",VERTEX,{"derivedFrom":[subQ0,sQuery(id+"F14.wireOp",EDGE,"E11.0.3.3")]}),1.0]])],"derivedFrom":subQ0})])],"isStart":false})});}
            var Q84;
            {var subQ0=sQuery(id+"F14.wireOp",EDGE,"E11.0.2.0");Q84=makeQuery(id+"F17.boolean.opBoolean","COPY",EDGE,{"derivedFrom":makeQuery(id+"F17.opExtrude","CAP_EDGE",EDGE,{"disambiguationData":[OSD([subQ0]),TDD([makeQuery(id+"F14.imprint","IMPRINT",EDGE,{"disambiguationData":[TD([[makeQuery(id+"F14.imprint","INTERSECT",VERTEX,{"derivedFrom":[subQ0,sQuery(id+"F14.wireOp",EDGE,"E11.0.2.3")]}),1.0]])],"derivedFrom":subQ0})])],"isStart":false})});}
            var Q85;
            {var subQ0=sQuery(id+"F14.wireOp",EDGE,"E11.0.2.1");Q85=makeQuery(id+"F17.boolean.opBoolean","COPY",EDGE,{"derivedFrom":makeQuery(id+"F17.opExtrude","CAP_EDGE",EDGE,{"disambiguationData":[OSD([subQ0]),TDD([makeQuery(id+"F14.imprint","IMPRINT",EDGE,{"disambiguationData":[TD([[makeQuery(id+"F14.imprint","INTERSECT",VERTEX,{"derivedFrom":[subQ0,sQuery(id+"F14.wireOp",EDGE,"E11.0.2.3")]}),1.0]])],"derivedFrom":subQ0})])],"isStart":false})});}
            var Q86;
            {var subQ0=sQuery(id+"F14.wireOp",EDGE,"E11.0.1.0");Q86=makeQuery(id+"F17.boolean.opBoolean","COPY",EDGE,{"derivedFrom":makeQuery(id+"F17.opExtrude","CAP_EDGE",EDGE,{"disambiguationData":[OSD([subQ0]),TDD([makeQuery(id+"F14.imprint","IMPRINT",EDGE,{"disambiguationData":[TD([[makeQuery(id+"F14.imprint","INTERSECT",VERTEX,{"derivedFrom":[subQ0,sQuery(id+"F14.wireOp",EDGE,"E11.0.1.3")]}),1.0]])],"derivedFrom":subQ0})])],"isStart":false})});}
            var Q87;
            {var subQ0=sQuery(id+"F14.wireOp",EDGE,"E11.0.1.1");Q87=makeQuery(id+"F17.boolean.opBoolean","COPY",EDGE,{"derivedFrom":makeQuery(id+"F17.opExtrude","CAP_EDGE",EDGE,{"disambiguationData":[OSD([subQ0]),TDD([makeQuery(id+"F14.imprint","IMPRINT",EDGE,{"disambiguationData":[TD([[makeQuery(id+"F14.imprint","INTERSECT",VERTEX,{"derivedFrom":[subQ0,sQuery(id+"F14.wireOp",EDGE,"E11.0.1.3")]}),1.0]])],"derivedFrom":subQ0})])],"isStart":false})});}
            var Q88;
            {var subQ0=sQuery(id+"F14.wireOp",EDGE,"E10.bottom");Q88=makeQuery(id+"F17.boolean.opBoolean","COPY",EDGE,{"derivedFrom":makeQuery(id+"F17.opExtrude","CAP_EDGE",EDGE,{"disambiguationData":[OSD([subQ0]),TDD([makeQuery(id+"F14.imprint","IMPRINT",EDGE,{"disambiguationData":[TD([[makeQuery(id+"F14.imprint","INTERSECT",VERTEX,{"derivedFrom":[subQ0,sQuery(id+"F14.wireOp",EDGE,"E10.right")]}),1.0]])],"derivedFrom":subQ0})])],"isStart":false})});}
            var Q89;
            {var subQ0=sQuery(id+"F14.wireOp",EDGE,"E10.top");Q89=makeQuery(id+"F17.boolean.opBoolean","COPY",EDGE,{"derivedFrom":makeQuery(id+"F17.opExtrude","CAP_EDGE",EDGE,{"disambiguationData":[OSD([subQ0]),TDD([makeQuery(id+"F14.imprint","IMPRINT",EDGE,{"disambiguationData":[TD([[makeQuery(id+"F14.imprint","INTERSECT",VERTEX,{"derivedFrom":[subQ0,sQuery(id+"F14.wireOp",EDGE,"E10.right")]}),1.0]])],"derivedFrom":subQ0})])],"isStart":false})});}
            var Q90;
            {var subQ0=sQuery(id+"F14.wireOp",EDGE,"E11.0.14.0");Q90=makeQuery(id+"F17.boolean.opBoolean","COPY",EDGE,{"derivedFrom":makeQuery(id+"F17.opExtrude","CAP_EDGE",EDGE,{"disambiguationData":[OSD([subQ0]),TDD([makeQuery(id+"F14.imprint","IMPRINT",EDGE,{"disambiguationData":[TD([[makeQuery(id+"F14.imprint","INTERSECT",VERTEX,{"derivedFrom":[subQ0,sQuery(id+"F14.wireOp",EDGE,"E11.0.14.2")]}),-1.0]])],"derivedFrom":subQ0})])],"isStart":false})});}
            var Q91;
            {var subQ0=sQuery(id+"F14.wireOp",EDGE,"E11.0.14.1");Q91=makeQuery(id+"F17.boolean.opBoolean","COPY",EDGE,{"derivedFrom":makeQuery(id+"F17.opExtrude","CAP_EDGE",EDGE,{"disambiguationData":[OSD([subQ0]),TDD([makeQuery(id+"F14.imprint","IMPRINT",EDGE,{"disambiguationData":[TD([[makeQuery(id+"F14.imprint","INTERSECT",VERTEX,{"derivedFrom":[subQ0,sQuery(id+"F14.wireOp",EDGE,"E11.0.14.2")]}),-1.0]])],"derivedFrom":subQ0})])],"isStart":false})});}
            var Q92;
            {var subQ0=sQuery(id+"F14.wireOp",EDGE,"E11.0.13.1");Q92=makeQuery(id+"F17.boolean.opBoolean","COPY",EDGE,{"derivedFrom":makeQuery(id+"F17.opExtrude","CAP_EDGE",EDGE,{"disambiguationData":[OSD([subQ0]),TDD([makeQuery(id+"F14.imprint","IMPRINT",EDGE,{"disambiguationData":[TD([[makeQuery(id+"F14.imprint","INTERSECT",VERTEX,{"derivedFrom":[subQ0,sQuery(id+"F14.wireOp",EDGE,"E11.0.13.2")]}),-1.0]])],"derivedFrom":subQ0})])],"isStart":false})});}
            var Q93;
            {var subQ0=sQuery(id+"F14.wireOp",EDGE,"E11.0.13.0");Q93=makeQuery(id+"F17.boolean.opBoolean","COPY",EDGE,{"derivedFrom":makeQuery(id+"F17.opExtrude","CAP_EDGE",EDGE,{"disambiguationData":[OSD([subQ0]),TDD([makeQuery(id+"F14.imprint","IMPRINT",EDGE,{"disambiguationData":[TD([[makeQuery(id+"F14.imprint","INTERSECT",VERTEX,{"derivedFrom":[subQ0,sQuery(id+"F14.wireOp",EDGE,"E11.0.13.2")]}),-1.0]])],"derivedFrom":subQ0})])],"isStart":false})});}
            var Q94;
            {var subQ0=sQuery(id+"F14.wireOp",EDGE,"E11.0.12.1");Q94=makeQuery(id+"F17.boolean.opBoolean","COPY",EDGE,{"derivedFrom":makeQuery(id+"F17.opExtrude","CAP_EDGE",EDGE,{"disambiguationData":[OSD([subQ0]),TDD([makeQuery(id+"F14.imprint","IMPRINT",EDGE,{"disambiguationData":[TD([[makeQuery(id+"F14.imprint","INTERSECT",VERTEX,{"derivedFrom":[subQ0,sQuery(id+"F14.wireOp",EDGE,"E11.0.12.2")]}),-1.0]])],"derivedFrom":subQ0})])],"isStart":false})});}
            var Q95;
            {var subQ0=sQuery(id+"F14.wireOp",EDGE,"E11.0.12.0");Q95=makeQuery(id+"F17.boolean.opBoolean","COPY",EDGE,{"derivedFrom":makeQuery(id+"F17.opExtrude","CAP_EDGE",EDGE,{"disambiguationData":[OSD([subQ0]),TDD([makeQuery(id+"F14.imprint","IMPRINT",EDGE,{"disambiguationData":[TD([[makeQuery(id+"F14.imprint","INTERSECT",VERTEX,{"derivedFrom":[subQ0,sQuery(id+"F14.wireOp",EDGE,"E11.0.12.2")]}),-1.0]])],"derivedFrom":subQ0})])],"isStart":false})});}
            var Q96;
            {var subQ0=sQuery(id+"F14.wireOp",EDGE,"E11.0.11.0");Q96=makeQuery(id+"F17.boolean.opBoolean","COPY",EDGE,{"derivedFrom":makeQuery(id+"F17.opExtrude","CAP_EDGE",EDGE,{"disambiguationData":[OSD([subQ0]),TDD([makeQuery(id+"F14.imprint","IMPRINT",EDGE,{"disambiguationData":[TD([[makeQuery(id+"F14.imprint","INTERSECT",VERTEX,{"derivedFrom":[subQ0,sQuery(id+"F14.wireOp",EDGE,"E11.0.11.2")]}),-1.0]])],"derivedFrom":subQ0})])],"isStart":false})});}
            var Q97;
            {var subQ0=sQuery(id+"F14.wireOp",EDGE,"E11.0.11.1");Q97=makeQuery(id+"F17.boolean.opBoolean","COPY",EDGE,{"derivedFrom":makeQuery(id+"F17.opExtrude","CAP_EDGE",EDGE,{"disambiguationData":[OSD([subQ0]),TDD([makeQuery(id+"F14.imprint","IMPRINT",EDGE,{"disambiguationData":[TD([[makeQuery(id+"F14.imprint","INTERSECT",VERTEX,{"derivedFrom":[subQ0,sQuery(id+"F14.wireOp",EDGE,"E11.0.11.2")]}),-1.0]])],"derivedFrom":subQ0})])],"isStart":false})});}
            var Q98;
            {var subQ0=sQuery(id+"F14.wireOp",EDGE,"E11.0.10.0");Q98=makeQuery(id+"F17.boolean.opBoolean","COPY",EDGE,{"derivedFrom":makeQuery(id+"F17.opExtrude","CAP_EDGE",EDGE,{"disambiguationData":[OSD([subQ0]),TDD([makeQuery(id+"F14.imprint","IMPRINT",EDGE,{"disambiguationData":[TD([[makeQuery(id+"F14.imprint","INTERSECT",VERTEX,{"derivedFrom":[subQ0,sQuery(id+"F14.wireOp",EDGE,"E11.0.10.2")]}),-1.0]])],"derivedFrom":subQ0})])],"isStart":false})});}
            var Q99;
            {var subQ0=sQuery(id+"F14.wireOp",EDGE,"E11.0.10.1");Q99=makeQuery(id+"F17.boolean.opBoolean","COPY",EDGE,{"derivedFrom":makeQuery(id+"F17.opExtrude","CAP_EDGE",EDGE,{"disambiguationData":[OSD([subQ0]),TDD([makeQuery(id+"F14.imprint","IMPRINT",EDGE,{"disambiguationData":[TD([[makeQuery(id+"F14.imprint","INTERSECT",VERTEX,{"derivedFrom":[subQ0,sQuery(id+"F14.wireOp",EDGE,"E11.0.10.2")]}),-1.0]])],"derivedFrom":subQ0})])],"isStart":false})});}
            var Q100;
            {var subQ0=sQuery(id+"F14.wireOp",EDGE,"E11.0.9.0");Q100=makeQuery(id+"F17.boolean.opBoolean","COPY",EDGE,{"derivedFrom":makeQuery(id+"F17.opExtrude","CAP_EDGE",EDGE,{"disambiguationData":[OSD([subQ0]),TDD([makeQuery(id+"F14.imprint","IMPRINT",EDGE,{"disambiguationData":[TD([[makeQuery(id+"F14.imprint","INTERSECT",VERTEX,{"derivedFrom":[subQ0,sQuery(id+"F14.wireOp",EDGE,"E11.0.9.2")]}),-1.0]])],"derivedFrom":subQ0})])],"isStart":false})});}
            var Q101;
            {var subQ0=sQuery(id+"F14.wireOp",EDGE,"E11.0.9.1");Q101=makeQuery(id+"F17.boolean.opBoolean","COPY",EDGE,{"derivedFrom":makeQuery(id+"F17.opExtrude","CAP_EDGE",EDGE,{"disambiguationData":[OSD([subQ0]),TDD([makeQuery(id+"F14.imprint","IMPRINT",EDGE,{"disambiguationData":[TD([[makeQuery(id+"F14.imprint","INTERSECT",VERTEX,{"derivedFrom":[subQ0,sQuery(id+"F14.wireOp",EDGE,"E11.0.9.2")]}),-1.0]])],"derivedFrom":subQ0})])],"isStart":false})});}
            var Q102;
            {var subQ0=sQuery(id+"F14.wireOp",EDGE,"E11.0.8.1");Q102=makeQuery(id+"F17.boolean.opBoolean","COPY",EDGE,{"derivedFrom":makeQuery(id+"F17.opExtrude","CAP_EDGE",EDGE,{"disambiguationData":[OSD([subQ0]),TDD([makeQuery(id+"F14.imprint","IMPRINT",EDGE,{"disambiguationData":[TD([[makeQuery(id+"F14.imprint","INTERSECT",VERTEX,{"derivedFrom":[subQ0,sQuery(id+"F14.wireOp",EDGE,"E11.0.8.2")]}),-1.0]])],"derivedFrom":subQ0})])],"isStart":false})});}
            var Q103;
            {var subQ0=sQuery(id+"F14.wireOp",EDGE,"E11.0.8.0");Q103=makeQuery(id+"F17.boolean.opBoolean","COPY",EDGE,{"derivedFrom":makeQuery(id+"F17.opExtrude","CAP_EDGE",EDGE,{"disambiguationData":[OSD([subQ0]),TDD([makeQuery(id+"F14.imprint","IMPRINT",EDGE,{"disambiguationData":[TD([[makeQuery(id+"F14.imprint","INTERSECT",VERTEX,{"derivedFrom":[subQ0,sQuery(id+"F14.wireOp",EDGE,"E11.0.8.2")]}),-1.0]])],"derivedFrom":subQ0})])],"isStart":false})});}
            var Q104;
            {var subQ0=sQuery(id+"F14.wireOp",EDGE,"E11.0.6.0");Q104=makeQuery(id+"F17.boolean.opBoolean","COPY",EDGE,{"derivedFrom":makeQuery(id+"F17.opExtrude","CAP_EDGE",EDGE,{"disambiguationData":[OSD([subQ0]),TDD([makeQuery(id+"F14.imprint","IMPRINT",EDGE,{"disambiguationData":[TD([[makeQuery(id+"F14.imprint","INTERSECT",VERTEX,{"derivedFrom":[subQ0,sQuery(id+"F14.wireOp",EDGE,"E11.0.6.2")]}),-1.0]])],"derivedFrom":subQ0})])],"isStart":false})});}
            var Q105;
            {var subQ0=sQuery(id+"F14.wireOp",EDGE,"E11.0.6.1");Q105=makeQuery(id+"F17.boolean.opBoolean","COPY",EDGE,{"derivedFrom":makeQuery(id+"F17.opExtrude","CAP_EDGE",EDGE,{"disambiguationData":[OSD([subQ0]),TDD([makeQuery(id+"F14.imprint","IMPRINT",EDGE,{"disambiguationData":[TD([[makeQuery(id+"F14.imprint","INTERSECT",VERTEX,{"derivedFrom":[subQ0,sQuery(id+"F14.wireOp",EDGE,"E11.0.6.2")]}),-1.0]])],"derivedFrom":subQ0})])],"isStart":false})});}
            var Q106;
            {var subQ0=sQuery(id+"F14.wireOp",EDGE,"E11.0.7.0");Q106=makeQuery(id+"F17.boolean.opBoolean","COPY",EDGE,{"derivedFrom":makeQuery(id+"F17.opExtrude","CAP_EDGE",EDGE,{"disambiguationData":[OSD([subQ0]),TDD([makeQuery(id+"F14.imprint","IMPRINT",EDGE,{"disambiguationData":[TD([[makeQuery(id+"F14.imprint","INTERSECT",VERTEX,{"derivedFrom":[subQ0,sQuery(id+"F14.wireOp",EDGE,"E11.0.7.2")]}),-1.0]])],"derivedFrom":subQ0})])],"isStart":false})});}
            var Q107;
            {var subQ0=sQuery(id+"F14.wireOp",EDGE,"E11.0.7.1");Q107=makeQuery(id+"F17.boolean.opBoolean","COPY",EDGE,{"derivedFrom":makeQuery(id+"F17.opExtrude","CAP_EDGE",EDGE,{"disambiguationData":[OSD([subQ0]),TDD([makeQuery(id+"F14.imprint","IMPRINT",EDGE,{"disambiguationData":[TD([[makeQuery(id+"F14.imprint","INTERSECT",VERTEX,{"derivedFrom":[subQ0,sQuery(id+"F14.wireOp",EDGE,"E11.0.7.2")]}),-1.0]])],"derivedFrom":subQ0})])],"isStart":false})});}
            var Q108;
            {var subQ0=sQuery(id+"F14.wireOp",EDGE,"E11.0.5.1");Q108=makeQuery(id+"F17.boolean.opBoolean","COPY",EDGE,{"derivedFrom":makeQuery(id+"F17.opExtrude","CAP_EDGE",EDGE,{"disambiguationData":[OSD([subQ0]),TDD([makeQuery(id+"F14.imprint","IMPRINT",EDGE,{"disambiguationData":[TD([[makeQuery(id+"F14.imprint","INTERSECT",VERTEX,{"derivedFrom":[subQ0,sQuery(id+"F14.wireOp",EDGE,"E11.0.5.2")]}),-1.0]])],"derivedFrom":subQ0})])],"isStart":false})});}
            var Q109;
            {var subQ0=sQuery(id+"F14.wireOp",EDGE,"E11.0.5.0");Q109=makeQuery(id+"F17.boolean.opBoolean","COPY",EDGE,{"derivedFrom":makeQuery(id+"F17.opExtrude","CAP_EDGE",EDGE,{"disambiguationData":[OSD([subQ0]),TDD([makeQuery(id+"F14.imprint","IMPRINT",EDGE,{"disambiguationData":[TD([[makeQuery(id+"F14.imprint","INTERSECT",VERTEX,{"derivedFrom":[subQ0,sQuery(id+"F14.wireOp",EDGE,"E11.0.5.2")]}),-1.0]])],"derivedFrom":subQ0})])],"isStart":false})});}
            var Q110;
            {var subQ0=sQuery(id+"F14.wireOp",EDGE,"E11.0.4.0");Q110=makeQuery(id+"F17.boolean.opBoolean","COPY",EDGE,{"derivedFrom":makeQuery(id+"F17.opExtrude","CAP_EDGE",EDGE,{"disambiguationData":[OSD([subQ0]),TDD([makeQuery(id+"F14.imprint","IMPRINT",EDGE,{"disambiguationData":[TD([[makeQuery(id+"F14.imprint","INTERSECT",VERTEX,{"derivedFrom":[subQ0,sQuery(id+"F14.wireOp",EDGE,"E11.0.4.2")]}),-1.0]])],"derivedFrom":subQ0})])],"isStart":false})});}
            var Q111;
            {var subQ0=sQuery(id+"F14.wireOp",EDGE,"E11.0.4.1");Q111=makeQuery(id+"F17.boolean.opBoolean","COPY",EDGE,{"derivedFrom":makeQuery(id+"F17.opExtrude","CAP_EDGE",EDGE,{"disambiguationData":[OSD([subQ0]),TDD([makeQuery(id+"F14.imprint","IMPRINT",EDGE,{"disambiguationData":[TD([[makeQuery(id+"F14.imprint","INTERSECT",VERTEX,{"derivedFrom":[subQ0,sQuery(id+"F14.wireOp",EDGE,"E11.0.4.2")]}),-1.0]])],"derivedFrom":subQ0})])],"isStart":false})});}
            var Q112;
            {var subQ0=sQuery(id+"F14.wireOp",EDGE,"E11.0.3.0");Q112=makeQuery(id+"F17.boolean.opBoolean","COPY",EDGE,{"derivedFrom":makeQuery(id+"F17.opExtrude","CAP_EDGE",EDGE,{"disambiguationData":[OSD([subQ0]),TDD([makeQuery(id+"F14.imprint","IMPRINT",EDGE,{"disambiguationData":[TD([[makeQuery(id+"F14.imprint","INTERSECT",VERTEX,{"derivedFrom":[subQ0,sQuery(id+"F14.wireOp",EDGE,"E11.0.3.2")]}),-1.0]])],"derivedFrom":subQ0})])],"isStart":false})});}
            var Q113;
            {var subQ0=sQuery(id+"F14.wireOp",EDGE,"E11.0.3.1");Q113=makeQuery(id+"F17.boolean.opBoolean","COPY",EDGE,{"derivedFrom":makeQuery(id+"F17.opExtrude","CAP_EDGE",EDGE,{"disambiguationData":[OSD([subQ0]),TDD([makeQuery(id+"F14.imprint","IMPRINT",EDGE,{"disambiguationData":[TD([[makeQuery(id+"F14.imprint","INTERSECT",VERTEX,{"derivedFrom":[subQ0,sQuery(id+"F14.wireOp",EDGE,"E11.0.3.2")]}),-1.0]])],"derivedFrom":subQ0})])],"isStart":false})});}
            var Q114;
            {var subQ0=sQuery(id+"F14.wireOp",EDGE,"E11.0.2.0");Q114=makeQuery(id+"F17.boolean.opBoolean","COPY",EDGE,{"derivedFrom":makeQuery(id+"F17.opExtrude","CAP_EDGE",EDGE,{"disambiguationData":[OSD([subQ0]),TDD([makeQuery(id+"F14.imprint","IMPRINT",EDGE,{"disambiguationData":[TD([[makeQuery(id+"F14.imprint","INTERSECT",VERTEX,{"derivedFrom":[subQ0,sQuery(id+"F14.wireOp",EDGE,"E11.0.2.2")]}),-1.0]])],"derivedFrom":subQ0})])],"isStart":false})});}
            var Q115;
            {var subQ0=sQuery(id+"F14.wireOp",EDGE,"E11.0.2.1");Q115=makeQuery(id+"F17.boolean.opBoolean","COPY",EDGE,{"derivedFrom":makeQuery(id+"F17.opExtrude","CAP_EDGE",EDGE,{"disambiguationData":[OSD([subQ0]),TDD([makeQuery(id+"F14.imprint","IMPRINT",EDGE,{"disambiguationData":[TD([[makeQuery(id+"F14.imprint","INTERSECT",VERTEX,{"derivedFrom":[subQ0,sQuery(id+"F14.wireOp",EDGE,"E11.0.2.2")]}),-1.0]])],"derivedFrom":subQ0})])],"isStart":false})});}
            var Q116;
            {var subQ0=sQuery(id+"F14.wireOp",EDGE,"E11.0.1.0");Q116=makeQuery(id+"F17.boolean.opBoolean","COPY",EDGE,{"derivedFrom":makeQuery(id+"F17.opExtrude","CAP_EDGE",EDGE,{"disambiguationData":[OSD([subQ0]),TDD([makeQuery(id+"F14.imprint","IMPRINT",EDGE,{"disambiguationData":[TD([[makeQuery(id+"F14.imprint","INTERSECT",VERTEX,{"derivedFrom":[subQ0,sQuery(id+"F14.wireOp",EDGE,"E11.0.1.2")]}),-1.0]])],"derivedFrom":subQ0})])],"isStart":false})});}
            var Q117;
            {var subQ0=sQuery(id+"F14.wireOp",EDGE,"E11.0.1.1");Q117=makeQuery(id+"F17.boolean.opBoolean","COPY",EDGE,{"derivedFrom":makeQuery(id+"F17.opExtrude","CAP_EDGE",EDGE,{"disambiguationData":[OSD([subQ0]),TDD([makeQuery(id+"F14.imprint","IMPRINT",EDGE,{"disambiguationData":[TD([[makeQuery(id+"F14.imprint","INTERSECT",VERTEX,{"derivedFrom":[subQ0,sQuery(id+"F14.wireOp",EDGE,"E11.0.1.2")]}),-1.0]])],"derivedFrom":subQ0})])],"isStart":false})});}
            var Q118;
            {var subQ0=sQuery(id+"F14.wireOp",EDGE,"E10.bottom");Q118=makeQuery(id+"F17.boolean.opBoolean","COPY",EDGE,{"derivedFrom":makeQuery(id+"F17.opExtrude","CAP_EDGE",EDGE,{"disambiguationData":[OSD([subQ0]),TDD([makeQuery(id+"F14.imprint","IMPRINT",EDGE,{"disambiguationData":[TD([[makeQuery(id+"F14.imprint","INTERSECT",VERTEX,{"derivedFrom":[subQ0,sQuery(id+"F14.wireOp",EDGE,"E10.left")]}),-1.0]])],"derivedFrom":subQ0})])],"isStart":false})});}
            var Q119;
            {var subQ0=sQuery(id+"F14.wireOp",EDGE,"E10.top");Q119=makeQuery(id+"F17.boolean.opBoolean","COPY",EDGE,{"derivedFrom":makeQuery(id+"F17.opExtrude","CAP_EDGE",EDGE,{"disambiguationData":[OSD([subQ0]),TDD([makeQuery(id+"F14.imprint","IMPRINT",EDGE,{"disambiguationData":[TD([[makeQuery(id+"F14.imprint","INTERSECT",VERTEX,{"derivedFrom":[subQ0,sQuery(id+"F14.wireOp",EDGE,"E10.left")]}),-1.0]])],"derivedFrom":subQ0})])],"isStart":false})});}
            fillet(context, id + "F18", {"entities" : qUnion([Q0, Q1, Q2, Q3, Q4, Q5, Q6, Q7, Q8, Q9, Q10, Q11, Q12, Q13, Q14, Q15, Q16, Q17, Q18, Q19, Q20, Q21, Q22, Q23, Q24, Q25, Q26, Q27, Q28, Q29, Q30, Q31, Q32, Q33, Q34, Q35, Q36, Q37, Q38, Q39, Q40, Q41, Q42, Q43, Q44, Q45, Q46, Q47, Q48, Q49, Q50, Q51, Q52, Q53, Q54, Q55, Q56, Q57, Q58, Q59, Q60, Q61, Q62, Q63, Q64, Q65, Q66, Q67, Q68, Q69, Q70, Q71, Q72, Q73, Q74, Q75, Q76, Q77, Q78, Q79, Q80, Q81, Q82, Q83, Q84, Q85, Q86, Q87, Q88, Q89, Q90, Q91, Q92, Q93, Q94, Q95, Q96, Q97, Q98, Q99, Q100, Q101, Q102, Q103, Q104, Q105, Q106, Q107, Q108, Q109, Q110, Q111, Q112, Q113, Q114, Q115, Q116, Q117, Q118, Q119]), "radius" : 2.5 * mm, "tangentPropagation" : true, "allowEdgeOverflow" : false});
        }
        {
            var Q0;
            {var subQ0=sQuery(id+"F0.wireOp",EDGE,"E0.left");var subQ3=sQuery(id+"F0.wireOp",EDGE,"E0.bottom");Q0=makeQuery(id+"F11.boolean.opBoolean","SPLIT",FACE,{"disambiguationData":[TD([makeQuery(id+"F6.opExtrude","CAP_FACE",FACE,{"disambiguationData":[OSD([subQ0])],"isStart":false})])],"derivedFrom":makeQuery(id+"F6.boolean.opBoolean","MERGE",FACE,{"derivedFrom":[makeQuery(id+"F1.opExtrude","SWEPT_FACE",FACE,{"disambiguationData":[OSD([subQ3])]}),makeQuery(id+"F6.opExtrude","SWEPT_FACE",FACE,{"disambiguationData":[OSD([subQ3,subQ0])]})]})});}
            extrude(context, id + "F19", {"entities" : qUnion([Q0]), "operationType" : NewBodyOperationType.ADD, "depth" : 147.5 * mm});
        }
        {
            var Q0;
            {var subQ0=sQuery(id+"F0.wireOp",EDGE,"E0.left");var subQ2=sQuery(id+"F0.wireOp",EDGE,"E0.top");Q0=makeQuery(id+"F11.boolean.opBoolean","SPLIT",FACE,{"disambiguationData":[TD([makeQuery(id+"F6.opExtrude","CAP_FACE",FACE,{"disambiguationData":[OSD([subQ0])],"isStart":false})])],"derivedFrom":makeQuery(id+"F6.boolean.opBoolean","MERGE",FACE,{"derivedFrom":[makeQuery(id+"F1.opExtrude","SWEPT_FACE",FACE,{"disambiguationData":[OSD([subQ2])]}),makeQuery(id+"F6.opExtrude","SWEPT_FACE",FACE,{"disambiguationData":[OSD([subQ2,subQ0])]})]})});}
            extrude(context, id + "F20", {"entities" : qUnion([Q0]), "operationType" : NewBodyOperationType.ADD, "depth" : 147.5 * mm});
        }
        {
            var Q0;
            {var subQ0=sQuery(id+"F0.wireOp",EDGE,"E0.right");var subQ1=sQuery(id+"F0.wireOp",EDGE,"E0.left");var subQ2=sQuery(id+"F10.wireOp",EDGE,"E5.right");var subQ5=sQuery(id+"F10.wireOp",EDGE,"E5.bottom");var subQ9=sQuery(id+"F0.wireOp",EDGE,"E0.bottom");var subQ13=makeQuery(id+"F11.opExtrude","SWEPT_FACE",FACE,{"disambiguationData":[OSD([subQ2])]});Q0=makeQuery(id+"F19.boolean.opBoolean","MERGE",FACE,{"derivedFrom":[makeQuery(id+"F16.boolean.opBoolean","SPLIT",FACE,{"disambiguationData":[TD([subQ13])],"derivedFrom":makeQuery(id+"F11.opExtrude","SWEPT_FACE",FACE,{"disambiguationData":[OSD([subQ5])]})}),makeQuery(id+"F19.opExtrude","CAP_FACE",FACE,{"disambiguationData":[OSD([subQ9,subQ1]),TDD([makeQuery(id+"F16.boolean.opBoolean","SPLIT",FACE,{"disambiguationData":[TD([makeQuery(id+"F1.opExtrude","SWEPT_FACE",FACE,{"disambiguationData":[OSD([subQ0])]})])],"derivedFrom":makeQuery(id+"F6.boolean.opBoolean","MERGE",FACE,{"derivedFrom":[makeQuery(id+"F1.opExtrude","SWEPT_FACE",FACE,{"disambiguationData":[OSD([subQ9])]}),makeQuery(id+"F6.opExtrude","SWEPT_FACE",FACE,{"disambiguationData":[OSD([subQ9,subQ1])]})]})})])],"isStart":false})]});}
            var sketch = newSketch(context, id + "F21", { "sketchPlane" : qUnion([Q0])});
            skLineSegment(sketch, "E13.bottom", {"start": v(-100, 20) * mm, "end": v(93, 20) * mm});
            skLineSegment(sketch, "E13.top", {"start": v(-100, 0) * mm, "end": v(93, 0) * mm});
            skLineSegment(sketch, "E13.left", {"start": v(-100, 20) * mm, "end": v(-100, 0) * mm});
            skLineSegment(sketch, "E13.right", {"start": v(93, 20) * mm, "end": v(93, 0) * mm});
            skSolve(sketch);
        }
        {
            var Q0;
            Q0 = qSketchRegion(id + "F21", true);
            extrude(context, id + "F22", {"entities" : qUnion([Q0]), "operationType" : NewBodyOperationType.REMOVE, "oppositeDirection" : true, "depth" : 145 * mm});
        }
        {
            var Q0;
            {var subQ0=sQuery(id+"F0.wireOp",EDGE,"E0.right");var subQ1=sQuery(id+"F0.wireOp",EDGE,"E0.left");var subQ2=sQuery(id+"F10.wireOp",EDGE,"E5.right");var subQ4=sQuery(id+"F10.wireOp",EDGE,"E5.top");var subQ8=sQuery(id+"F0.wireOp",EDGE,"E0.top");var subQ14=makeQuery(id+"F11.opExtrude","SWEPT_FACE",FACE,{"disambiguationData":[OSD([subQ2])]});Q0=makeQuery(id+"F20.boolean.opBoolean","MERGE",FACE,{"derivedFrom":[makeQuery(id+"F13.boolean.opBoolean","SPLIT",FACE,{"disambiguationData":[TD([subQ14])],"derivedFrom":makeQuery(id+"F11.opExtrude","SWEPT_FACE",FACE,{"disambiguationData":[OSD([subQ4])]})}),makeQuery(id+"F20.opExtrude","CAP_FACE",FACE,{"disambiguationData":[OSD([subQ8,subQ1]),TDD([makeQuery(id+"F13.boolean.opBoolean","SPLIT",FACE,{"disambiguationData":[TD([makeQuery(id+"F1.opExtrude","SWEPT_FACE",FACE,{"disambiguationData":[OSD([subQ0])]})])],"derivedFrom":makeQuery(id+"F6.boolean.opBoolean","MERGE",FACE,{"derivedFrom":[makeQuery(id+"F1.opExtrude","SWEPT_FACE",FACE,{"disambiguationData":[OSD([subQ8])]}),makeQuery(id+"F6.opExtrude","SWEPT_FACE",FACE,{"disambiguationData":[OSD([subQ8,subQ1])]})]})})])],"isStart":false})]});}
            var sketch = newSketch(context, id + "F23", { "sketchPlane" : qUnion([Q0])});
            skLineSegment(sketch, "E14.bottom", {"start": v(100, 0) * mm, "end": v(-93, 0) * mm});
            skLineSegment(sketch, "E14.top", {"start": v(100, 20) * mm, "end": v(-93, 20) * mm});
            skLineSegment(sketch, "E14.left", {"start": v(100, 0) * mm, "end": v(100, 20) * mm});
            skLineSegment(sketch, "E14.right", {"start": v(-93, 0) * mm, "end": v(-93, 20) * mm});
            skSolve(sketch);
        }
        {
            var Q0;
            Q0 = qSketchRegion(id + "F23", true);
            var Q1;
            Q1=makeQuery(id+"F23.imprint","IMPRINT",FACE,{"disambiguationData":[TD([[makeQuery(id+"F23.imprint","IMPRINT",EDGE,{"derivedFrom":sQuery(id+"F23.wireOp",EDGE,"E14.bottom")}),1.0]])]});
            extrude(context, id + "F24", {"entities" : qUnion([Q0, Q1]), "operationType" : NewBodyOperationType.REMOVE, "oppositeDirection" : true, "depth" : 145 * mm});
        }
        {
            var Q0;
            {var subQ0=sQuery(id+"F0.wireOp",EDGE,"E0.left");var subQ1=sQuery(id+"F0.wireOp",EDGE,"E0.top");var subQ3=sQuery(id+"F10.wireOp",EDGE,"E5.right");var subQ4=sQuery(id+"F10.wireOp",EDGE,"E5.left");var subQ5=makeQuery(id+"F11.opExtrude","CAP_FACE",FACE,{"disambiguationData":[OSD([sQuery(id+"F7.wireOp",EDGE,"E3"),sQuery(id+"F10.wireOp",EDGE,"E5.bottom"),sQuery(id+"F10.wireOp",EDGE,"E5.top"),subQ4,subQ3])],"isStart":true});var subQ7=makeQuery(id+"F6.opExtrude","SWEPT_FACE",FACE,{"disambiguationData":[OSD([subQ0]),TDD([makeQuery(id+"F1.opExtrude","CAP_EDGE",EDGE,{"disambiguationData":[OSD([subQ0])],"isStart":false})])]});var subQ8=sQuery(id+"F0.wireOp",EDGE,"E0.right");var subQ9=sQuery(id+"F0.wireOp",EDGE,"E0.bottom");var subQ10=makeQuery(id+"F1.opExtrude","CAP_FACE",FACE,{"disambiguationData":[OSD([subQ9,subQ1,subQ0,subQ8])],"isStart":false});var subQ11=makeQuery(id+"F6.opExtrude","CAP_FACE",FACE,{"disambiguationData":[OSD([subQ0])],"isStart":false});var subQ13=makeQuery(id+"F6.boolean.opBoolean","MERGE",EDGE,{"derivedFrom":[makeQuery(id+"F1.opExtrude","CAP_EDGE",EDGE,{"disambiguationData":[OSD([subQ1])],"isStart":false}),makeQuery(id+"F6.opExtrude","SWEPT_EDGE",EDGE,{"disambiguationData":[OSD([subQ1,subQ0]),TDD([makeQuery(id+"F1.opExtrude","CAP_VERTEX",VERTEX,{"disambiguationData":[OSD([subQ1,subQ0])],"isStart":false})])]})]});var subQ14=makeQuery(id+"F1.opExtrude","SWEPT_FACE",FACE,{"disambiguationData":[OSD([subQ8])]});var subQ18=makeQuery(id+"F6.boolean.opBoolean","MERGE",EDGE,{"derivedFrom":[makeQuery(id+"F1.opExtrude","CAP_EDGE",EDGE,{"disambiguationData":[OSD([subQ9])],"isStart":false}),makeQuery(id+"F6.opExtrude","SWEPT_EDGE",EDGE,{"disambiguationData":[OSD([subQ9,subQ0]),TDD([makeQuery(id+"F1.opExtrude","CAP_VERTEX",VERTEX,{"disambiguationData":[OSD([subQ9,subQ0])],"isStart":false})])]})]});Q0=makeQuery(id+"F20.boolean.opBoolean","MERGE",FACE,{"derivedFrom":[makeQuery(id+"F19.boolean.opBoolean","MERGE",FACE,{"derivedFrom":[makeQuery(id+"F11.boolean.opBoolean","MERGE",FACE,{"derivedFrom":[makeQuery(id+"F6.boolean.opBoolean","MERGE",FACE,{"derivedFrom":[subQ10,subQ7]}),subQ5]}),makeQuery(id+"F19.opExtrude","SWEPT_FACE",FACE,{"disambiguationData":[OSD([subQ9,subQ0]),TDD([makeQuery(id+"F11.boolean.opBoolean","SPLIT",EDGE,{"disambiguationData":[TD([subQ14])],"derivedFrom":subQ18})])]}),makeQuery(id+"F19.opExtrude","SWEPT_FACE",FACE,{"disambiguationData":[OSD([subQ9,subQ0]),TDD([makeQuery(id+"F11.boolean.opBoolean","SPLIT",EDGE,{"disambiguationData":[TD([subQ11])],"derivedFrom":subQ18})])]})]}),makeQuery(id+"F20.opExtrude","SWEPT_FACE",FACE,{"disambiguationData":[OSD([subQ1,subQ0]),TDD([makeQuery(id+"F11.boolean.opBoolean","SPLIT",EDGE,{"disambiguationData":[TD([subQ14])],"derivedFrom":subQ13})])]}),makeQuery(id+"F20.opExtrude","SWEPT_FACE",FACE,{"disambiguationData":[OSD([subQ1,subQ0]),TDD([makeQuery(id+"F11.boolean.opBoolean","SPLIT",EDGE,{"disambiguationData":[TD([subQ11])],"derivedFrom":subQ13})])]})]});}
            var sketch = newSketch(context, id + "F25", { "sketchPlane" : qUnion([Q0])});
            skLineSegment(sketch, "E15", {"start": v(122.5, 275) * mm, "end": v(122.5, -275) * mm, "construction": true});
            skPoint(sketch, "E15.endSnap0", {"position": v(117.75, -275) * mm});
            skLineSegment(sketch, "E16", {"start": v(232.5, -275) * mm, "end": v(232.5, 275) * mm, "construction": true});
            skPoint(sketch, "E17", {"position": v(122.5, 255) * mm});
            skPoint(sketch, "E18", {"position": v(232.5, 255) * mm});
            skPoint(sketch, "E19.0.1.0", {"position": v(122.5, 205) * mm});
            skPoint(sketch, "E19.0.1.1", {"position": v(232.5, 205) * mm});
            skPoint(sketch, "E19.0.2.0", {"position": v(122.5, 155) * mm});
            skPoint(sketch, "E19.0.2.1", {"position": v(232.5, 155) * mm});
            skPoint(sketch, "E19.0.3.0", {"position": v(122.5, 105) * mm});
            skPoint(sketch, "E19.0.3.1", {"position": v(232.5, 105) * mm});
            skLineSegment(sketch, "E19.direction1", {"start": v(122.5, 255) * mm, "end": v(147.5, 255) * mm, "construction": true});
            skLineSegment(sketch, "E19.direction2", {"start": v(122.5, 255) * mm, "end": v(122.5, 205) * mm, "construction": true});
            skPoint(sketch, "E20", {"position": v(122.5, -255) * mm});
            skPoint(sketch, "E21", {"position": v(232.5, -255) * mm});
            skPoint(sketch, "E22.0.1.0", {"position": v(122.5, -205) * mm});
            skPoint(sketch, "E22.0.1.1", {"position": v(232.5, -205) * mm});
            skPoint(sketch, "E22.0.2.0", {"position": v(122.5, -155) * mm});
            skPoint(sketch, "E22.0.2.1", {"position": v(232.5, -155) * mm});
            skPoint(sketch, "E22.0.3.0", {"position": v(122.5, -105) * mm});
            skPoint(sketch, "E22.0.3.1", {"position": v(232.5, -105) * mm});
            skLineSegment(sketch, "E22.direction1", {"start": v(122.5, -255) * mm, "end": v(147.5, -255) * mm, "construction": true});
            skLineSegment(sketch, "E22.direction2", {"start": v(122.5, -255) * mm, "end": v(122.5, -205) * mm, "construction": true});
            skSolve(sketch);
        }
        {
            var Q0;
            Q0=sQuery(id+"F25.wireOp",VERTEX,"E19.0.3.0");
            var Q1;
            Q1=sQuery(id+"F25.wireOp",VERTEX,"E19.0.3.1");
            var Q2;
            Q2=sQuery(id+"F25.wireOp",VERTEX,"E19.0.2.1");
            var Q3;
            Q3=sQuery(id+"F25.wireOp",VERTEX,"E19.0.2.0");
            var Q4;
            Q4=sQuery(id+"F25.wireOp",VERTEX,"E19.0.1.0");
            var Q5;
            Q5=sQuery(id+"F25.wireOp",VERTEX,"E19.0.1.1");
            var Q6;
            Q6=sQuery(id+"F25.wireOp",VERTEX,"E18");
            var Q7;
            Q7=sQuery(id+"F25.wireOp",VERTEX,"E17");
            var Q8;
            Q8=sQuery(id+"F25.wireOp",VERTEX,"E20");
            var Q9;
            Q9=sQuery(id+"F25.wireOp",VERTEX,"E21");
            var Q10;
            Q10=sQuery(id+"F25.wireOp",VERTEX,"E22.0.1.1");
            var Q11;
            Q11=sQuery(id+"F25.wireOp",VERTEX,"E22.0.1.0");
            var Q12;
            Q12=sQuery(id+"F25.wireOp",VERTEX,"E22.0.2.0");
            var Q13;
            Q13=sQuery(id+"F25.wireOp",VERTEX,"E22.0.2.1");
            var Q14;
            Q14=sQuery(id+"F25.wireOp",VERTEX,"E22.0.3.1");
            var Q15;
            Q15=sQuery(id+"F25.wireOp",VERTEX,"E22.0.3.0");
            var Q16;
            Q16=makeQuery(id+"F1.opExtrude","SWEPT_BODY",BODY,{"disambiguationData":[OSD([sQuery(id+"F0.wireOp",EDGE,"E0.bottom"),sQuery(id+"F0.wireOp",EDGE,"E0.top"),sQuery(id+"F0.wireOp",EDGE,"E0.left"),sQuery(id+"F0.wireOp",EDGE,"E0.right")])]});
            hole(context, id + "F26", {"style" : HoleStyle.SIMPLE, "endStyle" : HoleEndStyle.BLIND, "standardTappedOrClearance" : lookupTablePath({ "standard" : "ISO", "engagement" : "75%", "pitch" : "0.8 mm", "size" : "M5", "type" : "Tapped" }), "standardBlindInLast" : lookupTablePath({ "standard" : "ISO", "engagement" : "75%", "pitch" : "0.8 mm", "size" : "M5", "type" : "Tapped" }), "holeDiameter" : 4.2 * mm, "showTappedDepth" : true, "holeDepth" : 9.68 * mm, "isTappedThrough" : true, "tappedDepth" : 7.28 * mm, "tapClearance" : 3, "locations" : qUnion([Q0, Q1, Q2, Q3, Q4, Q5, Q6, Q7, Q8, Q9, Q10, Q11, Q12, Q13, Q14, Q15]), "scope" : qUnion([Q16]), "majorDiameter" : 5 * mm});
        }
        {
            var Q0;
            {var subQ0=sQuery(id+"F0.wireOp",EDGE,"E0.left");var subQ1=sQuery(id+"F0.wireOp",EDGE,"E0.top");var subQ3=sQuery(id+"F10.wireOp",EDGE,"E5.right");var subQ4=sQuery(id+"F10.wireOp",EDGE,"E5.left");var subQ5=makeQuery(id+"F11.opExtrude","CAP_FACE",FACE,{"disambiguationData":[OSD([sQuery(id+"F7.wireOp",EDGE,"E3"),sQuery(id+"F10.wireOp",EDGE,"E5.bottom"),sQuery(id+"F10.wireOp",EDGE,"E5.top"),subQ4,subQ3])],"isStart":true});var subQ7=makeQuery(id+"F6.opExtrude","SWEPT_FACE",FACE,{"disambiguationData":[OSD([subQ0]),TDD([makeQuery(id+"F1.opExtrude","CAP_EDGE",EDGE,{"disambiguationData":[OSD([subQ0])],"isStart":false})])]});var subQ8=sQuery(id+"F0.wireOp",EDGE,"E0.right");var subQ9=sQuery(id+"F0.wireOp",EDGE,"E0.bottom");var subQ10=makeQuery(id+"F1.opExtrude","CAP_FACE",FACE,{"disambiguationData":[OSD([subQ9,subQ1,subQ0,subQ8])],"isStart":false});var subQ11=makeQuery(id+"F6.opExtrude","CAP_FACE",FACE,{"disambiguationData":[OSD([subQ0])],"isStart":false});var subQ13=makeQuery(id+"F6.boolean.opBoolean","MERGE",EDGE,{"derivedFrom":[makeQuery(id+"F1.opExtrude","CAP_EDGE",EDGE,{"disambiguationData":[OSD([subQ1])],"isStart":false}),makeQuery(id+"F6.opExtrude","SWEPT_EDGE",EDGE,{"disambiguationData":[OSD([subQ1,subQ0]),TDD([makeQuery(id+"F1.opExtrude","CAP_VERTEX",VERTEX,{"disambiguationData":[OSD([subQ1,subQ0])],"isStart":false})])]})]});var subQ14=makeQuery(id+"F1.opExtrude","SWEPT_FACE",FACE,{"disambiguationData":[OSD([subQ8])]});var subQ18=makeQuery(id+"F6.boolean.opBoolean","MERGE",EDGE,{"derivedFrom":[makeQuery(id+"F1.opExtrude","CAP_EDGE",EDGE,{"disambiguationData":[OSD([subQ9])],"isStart":false}),makeQuery(id+"F6.opExtrude","SWEPT_EDGE",EDGE,{"disambiguationData":[OSD([subQ9,subQ0]),TDD([makeQuery(id+"F1.opExtrude","CAP_VERTEX",VERTEX,{"disambiguationData":[OSD([subQ9,subQ0])],"isStart":false})])]})]});Q0=makeQuery(id+"F20.boolean.opBoolean","MERGE",FACE,{"derivedFrom":[makeQuery(id+"F19.boolean.opBoolean","MERGE",FACE,{"derivedFrom":[makeQuery(id+"F11.boolean.opBoolean","MERGE",FACE,{"derivedFrom":[makeQuery(id+"F6.boolean.opBoolean","MERGE",FACE,{"derivedFrom":[subQ10,subQ7]}),subQ5]}),makeQuery(id+"F19.opExtrude","SWEPT_FACE",FACE,{"disambiguationData":[OSD([subQ9,subQ0]),TDD([makeQuery(id+"F11.boolean.opBoolean","SPLIT",EDGE,{"disambiguationData":[TD([subQ14])],"derivedFrom":subQ18})])]}),makeQuery(id+"F19.opExtrude","SWEPT_FACE",FACE,{"disambiguationData":[OSD([subQ9,subQ0]),TDD([makeQuery(id+"F11.boolean.opBoolean","SPLIT",EDGE,{"disambiguationData":[TD([subQ11])],"derivedFrom":subQ18})])]})]}),makeQuery(id+"F20.opExtrude","SWEPT_FACE",FACE,{"disambiguationData":[OSD([subQ1,subQ0]),TDD([makeQuery(id+"F11.boolean.opBoolean","SPLIT",EDGE,{"disambiguationData":[TD([subQ14])],"derivedFrom":subQ13})])]}),makeQuery(id+"F20.opExtrude","SWEPT_FACE",FACE,{"disambiguationData":[OSD([subQ1,subQ0]),TDD([makeQuery(id+"F11.boolean.opBoolean","SPLIT",EDGE,{"disambiguationData":[TD([subQ11])],"derivedFrom":subQ13})])]})]});}
            var sketch = newSketch(context, id + "F27", { "sketchPlane" : qUnion([Q0])});
            skLineSegment(sketch, "E23.bottom", {"start": v(90.34, -30) * mm, "end": v(85.34, -30) * mm});
            skLineSegment(sketch, "E23.top", {"start": v(90.34, 30) * mm, "end": v(85.34, 30) * mm});
            skLineSegment(sketch, "E23.left", {"start": v(90.34, -30) * mm, "end": v(90.34, 30) * mm});
            skLineSegment(sketch, "E23.right", {"start": v(85.34, -30) * mm, "end": v(85.34, 30) * mm});
            skPoint(sketch, "E23.middle", {"position": v(87.84, 0) * mm});
            skSolve(sketch);
        }
        {
            var Q0;
            Q0=makeQuery(id+"F27.imprint","IMPRINT",FACE,{"disambiguationData":[TD([[makeQuery(id+"F27.imprint","IMPRINT",EDGE,{"derivedFrom":sQuery(id+"F27.wireOp",EDGE,"E23.bottom")}),-1.0]])]});
            extrude(context, id + "F28", {"entities" : qUnion([Q0]), "operationType" : NewBodyOperationType.REMOVE, "oppositeDirection" : true, "depth" : 5 * mm});
        }
        {
            var Q0;
            {var subQ0=sQuery(id+"F0.wireOp",EDGE,"E0.left");var subQ1=sQuery(id+"F0.wireOp",EDGE,"E0.top");var subQ3=sQuery(id+"F10.wireOp",EDGE,"E5.right");var subQ4=sQuery(id+"F10.wireOp",EDGE,"E5.left");var subQ5=makeQuery(id+"F11.opExtrude","CAP_FACE",FACE,{"disambiguationData":[OSD([sQuery(id+"F7.wireOp",EDGE,"E3"),sQuery(id+"F10.wireOp",EDGE,"E5.bottom"),sQuery(id+"F10.wireOp",EDGE,"E5.top"),subQ4,subQ3])],"isStart":true});var subQ7=makeQuery(id+"F6.opExtrude","SWEPT_FACE",FACE,{"disambiguationData":[OSD([subQ0]),TDD([makeQuery(id+"F1.opExtrude","CAP_EDGE",EDGE,{"disambiguationData":[OSD([subQ0])],"isStart":false})])]});var subQ8=sQuery(id+"F0.wireOp",EDGE,"E0.right");var subQ9=sQuery(id+"F0.wireOp",EDGE,"E0.bottom");var subQ10=makeQuery(id+"F1.opExtrude","CAP_FACE",FACE,{"disambiguationData":[OSD([subQ9,subQ1,subQ0,subQ8])],"isStart":false});var subQ11=makeQuery(id+"F6.opExtrude","CAP_FACE",FACE,{"disambiguationData":[OSD([subQ0])],"isStart":false});var subQ13=makeQuery(id+"F6.boolean.opBoolean","MERGE",EDGE,{"derivedFrom":[makeQuery(id+"F1.opExtrude","CAP_EDGE",EDGE,{"disambiguationData":[OSD([subQ1])],"isStart":false}),makeQuery(id+"F6.opExtrude","SWEPT_EDGE",EDGE,{"disambiguationData":[OSD([subQ1,subQ0]),TDD([makeQuery(id+"F1.opExtrude","CAP_VERTEX",VERTEX,{"disambiguationData":[OSD([subQ1,subQ0])],"isStart":false})])]})]});var subQ14=makeQuery(id+"F1.opExtrude","SWEPT_FACE",FACE,{"disambiguationData":[OSD([subQ8])]});var subQ18=makeQuery(id+"F6.boolean.opBoolean","MERGE",EDGE,{"derivedFrom":[makeQuery(id+"F1.opExtrude","CAP_EDGE",EDGE,{"disambiguationData":[OSD([subQ9])],"isStart":false}),makeQuery(id+"F6.opExtrude","SWEPT_EDGE",EDGE,{"disambiguationData":[OSD([subQ9,subQ0]),TDD([makeQuery(id+"F1.opExtrude","CAP_VERTEX",VERTEX,{"disambiguationData":[OSD([subQ9,subQ0])],"isStart":false})])]})]});Q0=makeQuery(id+"F20.boolean.opBoolean","MERGE",FACE,{"derivedFrom":[makeQuery(id+"F19.boolean.opBoolean","MERGE",FACE,{"derivedFrom":[makeQuery(id+"F11.boolean.opBoolean","MERGE",FACE,{"derivedFrom":[makeQuery(id+"F6.boolean.opBoolean","MERGE",FACE,{"derivedFrom":[subQ10,subQ7]}),subQ5]}),makeQuery(id+"F19.opExtrude","SWEPT_FACE",FACE,{"disambiguationData":[OSD([subQ9,subQ0]),TDD([makeQuery(id+"F11.boolean.opBoolean","SPLIT",EDGE,{"disambiguationData":[TD([subQ14])],"derivedFrom":subQ18})])]}),makeQuery(id+"F19.opExtrude","SWEPT_FACE",FACE,{"disambiguationData":[OSD([subQ9,subQ0]),TDD([makeQuery(id+"F11.boolean.opBoolean","SPLIT",EDGE,{"disambiguationData":[TD([subQ11])],"derivedFrom":subQ18})])]})]}),makeQuery(id+"F20.opExtrude","SWEPT_FACE",FACE,{"disambiguationData":[OSD([subQ1,subQ0]),TDD([makeQuery(id+"F11.boolean.opBoolean","SPLIT",EDGE,{"disambiguationData":[TD([subQ14])],"derivedFrom":subQ13})])]}),makeQuery(id+"F20.opExtrude","SWEPT_FACE",FACE,{"disambiguationData":[OSD([subQ1,subQ0]),TDD([makeQuery(id+"F11.boolean.opBoolean","SPLIT",EDGE,{"disambiguationData":[TD([subQ11])],"derivedFrom":subQ13})])]})]});}
            var sketch = newSketch(context, id + "F29", { "sketchPlane" : qUnion([Q0])});
            skLineSegment(sketch, "E24.bottom", {"start": v(92.84, -25) * mm, "end": v(82.84, -25) * mm});
            skLineSegment(sketch, "E24.top", {"start": v(92.84, 25) * mm, "end": v(82.84, 25) * mm});
            skLineSegment(sketch, "E24.left", {"start": v(92.84, -25) * mm, "end": v(92.84, 25) * mm});
            skLineSegment(sketch, "E24.right", {"start": v(82.84, -25) * mm, "end": v(82.84, 25) * mm});
            skPoint(sketch, "E24.middle", {"position": v(87.84, 0) * mm});
            skPoint(sketch, "E24.middle.positionSnap0", {"position": v(87.84, 30) * mm});
            skPoint(sketch, "E24.middle.positionSnap1", {"position": v(90.34, 0) * mm});
            skPoint(sketch, "E24.centerSnap0", {"position": v(87.84, 30) * mm});
            skPoint(sketch, "E24.centerSnap1", {"position": v(90.34, 0) * mm});
            skSolve(sketch);
        }
        {
            var Q0;
            {var subQ0=sQuery(id+"F29.wireOp",EDGE,"E24.left");Q0=makeQuery(id+"F29.imprint","IMPRINT",FACE,{"disambiguationData":[TD([[makeQuery(id+"F29.imprint","IMPRINT",EDGE,{"derivedFrom":subQ0}),1.0]])]});}
            var Q1;
            {var subQ0=sQuery(id+"F29.wireOp",EDGE,"E24.right");Q1=makeQuery(id+"F29.imprint","IMPRINT",FACE,{"disambiguationData":[TD([[makeQuery(id+"F29.imprint","IMPRINT",EDGE,{"derivedFrom":subQ0}),-1.0]])]});}
            var Q2;
            {var subQ0=sQuery(id+"F29.wireOp",EDGE,"E24.bottom");var subQ1=makeQuery(id+"F28.boolean.opBoolean","COPY",EDGE,{"derivedFrom":makeQuery(id+"F28.opExtrude","CAP_EDGE",EDGE,{"disambiguationData":[OSD([sQuery(id+"F27.wireOp",EDGE,"E23.left")])],"isStart":true})});var subQ2=makeQuery(id+"F29.imprint","INTERSECT",VERTEX,{"derivedFrom":[subQ1,subQ0]});Q2=makeQuery(id+"F29.imprint","IMPRINT",FACE,{"disambiguationData":[TD([[makeQuery(id+"F29.imprint","IMPRINT",EDGE,{"disambiguationData":[TD([[subQ2,-1.0]])],"derivedFrom":subQ0}),-1.0]])]});}
            extrude(context, id + "F30", {"entities" : qUnion([Q0, Q1, Q2]), "operationType" : NewBodyOperationType.REMOVE, "oppositeDirection" : true, "depth" : 12 * mm});
        }
        {
            var Q0;
            {var subQ0=sQuery(id+"F27.wireOp",EDGE,"E23.left");var subQ1=sQuery(id+"F27.wireOp",EDGE,"E23.top");Q0=makeQuery(id+"F30.boolean.opBoolean","SPLIT",EDGE,{"disambiguationData":[TD([makeQuery(id+"F28.boolean.opBoolean","COPY",FACE,{"derivedFrom":makeQuery(id+"F28.opExtrude","SWEPT_FACE",FACE,{"disambiguationData":[OSD([subQ1])]})})])],"derivedFrom":makeQuery(id+"F28.boolean.opBoolean","COPY",EDGE,{"derivedFrom":makeQuery(id+"F28.opExtrude","CAP_EDGE",EDGE,{"disambiguationData":[OSD([subQ0])],"isStart":false})})});}
            var Q1;
            {var subQ0=sQuery(id+"F27.wireOp",EDGE,"E23.right");var subQ1=sQuery(id+"F27.wireOp",EDGE,"E23.top");Q1=makeQuery(id+"F30.boolean.opBoolean","SPLIT",EDGE,{"disambiguationData":[TD([makeQuery(id+"F28.boolean.opBoolean","COPY",FACE,{"derivedFrom":makeQuery(id+"F28.opExtrude","SWEPT_FACE",FACE,{"disambiguationData":[OSD([subQ1])]})})])],"derivedFrom":makeQuery(id+"F28.boolean.opBoolean","COPY",EDGE,{"derivedFrom":makeQuery(id+"F28.opExtrude","CAP_EDGE",EDGE,{"disambiguationData":[OSD([subQ0])],"isStart":false})})});}
            var Q2;
            {var subQ0=sQuery(id+"F27.wireOp",EDGE,"E23.bottom");var subQ1=sQuery(id+"F27.wireOp",EDGE,"E23.left");Q2=makeQuery(id+"F30.boolean.opBoolean","SPLIT",EDGE,{"disambiguationData":[TD([makeQuery(id+"F28.boolean.opBoolean","COPY",FACE,{"derivedFrom":makeQuery(id+"F28.opExtrude","SWEPT_FACE",FACE,{"disambiguationData":[OSD([subQ0])]})})])],"derivedFrom":makeQuery(id+"F28.boolean.opBoolean","COPY",EDGE,{"derivedFrom":makeQuery(id+"F28.opExtrude","CAP_EDGE",EDGE,{"disambiguationData":[OSD([subQ1])],"isStart":false})})});}
            var Q3;
            {var subQ0=sQuery(id+"F27.wireOp",EDGE,"E23.bottom");var subQ1=sQuery(id+"F27.wireOp",EDGE,"E23.right");Q3=makeQuery(id+"F30.boolean.opBoolean","SPLIT",EDGE,{"disambiguationData":[TD([makeQuery(id+"F28.boolean.opBoolean","COPY",FACE,{"derivedFrom":makeQuery(id+"F28.opExtrude","SWEPT_FACE",FACE,{"disambiguationData":[OSD([subQ0])]})})])],"derivedFrom":makeQuery(id+"F28.boolean.opBoolean","COPY",EDGE,{"derivedFrom":makeQuery(id+"F28.opExtrude","CAP_EDGE",EDGE,{"disambiguationData":[OSD([subQ1])],"isStart":false})})});}
            fillet(context, id + "F31", {"entities" : qUnion([Q0, Q1, Q2, Q3]), "radius" : 2.5 * mm, "tangentPropagation" : true, "allowEdgeOverflow" : false});
        }
        {
            var Q0;
            {var subQ0=sQuery(id+"F0.wireOp",EDGE,"E0.left");var subQ1=sQuery(id+"F0.wireOp",EDGE,"E0.top");var subQ3=sQuery(id+"F10.wireOp",EDGE,"E5.right");var subQ4=sQuery(id+"F10.wireOp",EDGE,"E5.left");var subQ5=makeQuery(id+"F11.opExtrude","CAP_FACE",FACE,{"disambiguationData":[OSD([sQuery(id+"F7.wireOp",EDGE,"E3"),sQuery(id+"F10.wireOp",EDGE,"E5.bottom"),sQuery(id+"F10.wireOp",EDGE,"E5.top"),subQ4,subQ3])],"isStart":true});var subQ7=makeQuery(id+"F6.opExtrude","SWEPT_FACE",FACE,{"disambiguationData":[OSD([subQ0]),TDD([makeQuery(id+"F1.opExtrude","CAP_EDGE",EDGE,{"disambiguationData":[OSD([subQ0])],"isStart":false})])]});var subQ8=sQuery(id+"F0.wireOp",EDGE,"E0.right");var subQ9=sQuery(id+"F0.wireOp",EDGE,"E0.bottom");var subQ10=makeQuery(id+"F1.opExtrude","CAP_FACE",FACE,{"disambiguationData":[OSD([subQ9,subQ1,subQ0,subQ8])],"isStart":false});var subQ11=makeQuery(id+"F6.opExtrude","CAP_FACE",FACE,{"disambiguationData":[OSD([subQ0])],"isStart":false});var subQ13=makeQuery(id+"F6.boolean.opBoolean","MERGE",EDGE,{"derivedFrom":[makeQuery(id+"F1.opExtrude","CAP_EDGE",EDGE,{"disambiguationData":[OSD([subQ1])],"isStart":false}),makeQuery(id+"F6.opExtrude","SWEPT_EDGE",EDGE,{"disambiguationData":[OSD([subQ1,subQ0]),TDD([makeQuery(id+"F1.opExtrude","CAP_VERTEX",VERTEX,{"disambiguationData":[OSD([subQ1,subQ0])],"isStart":false})])]})]});var subQ14=makeQuery(id+"F1.opExtrude","SWEPT_FACE",FACE,{"disambiguationData":[OSD([subQ8])]});var subQ18=makeQuery(id+"F6.boolean.opBoolean","MERGE",EDGE,{"derivedFrom":[makeQuery(id+"F1.opExtrude","CAP_EDGE",EDGE,{"disambiguationData":[OSD([subQ9])],"isStart":false}),makeQuery(id+"F6.opExtrude","SWEPT_EDGE",EDGE,{"disambiguationData":[OSD([subQ9,subQ0]),TDD([makeQuery(id+"F1.opExtrude","CAP_VERTEX",VERTEX,{"disambiguationData":[OSD([subQ9,subQ0])],"isStart":false})])]})]});Q0=makeQuery(id+"F20.boolean.opBoolean","MERGE",FACE,{"derivedFrom":[makeQuery(id+"F19.boolean.opBoolean","MERGE",FACE,{"derivedFrom":[makeQuery(id+"F11.boolean.opBoolean","MERGE",FACE,{"derivedFrom":[makeQuery(id+"F6.boolean.opBoolean","MERGE",FACE,{"derivedFrom":[subQ10,subQ7]}),subQ5]}),makeQuery(id+"F19.opExtrude","SWEPT_FACE",FACE,{"disambiguationData":[OSD([subQ9,subQ0]),TDD([makeQuery(id+"F11.boolean.opBoolean","SPLIT",EDGE,{"disambiguationData":[TD([subQ14])],"derivedFrom":subQ18})])]}),makeQuery(id+"F19.opExtrude","SWEPT_FACE",FACE,{"disambiguationData":[OSD([subQ9,subQ0]),TDD([makeQuery(id+"F11.boolean.opBoolean","SPLIT",EDGE,{"disambiguationData":[TD([subQ11])],"derivedFrom":subQ18})])]})]}),makeQuery(id+"F20.opExtrude","SWEPT_FACE",FACE,{"disambiguationData":[OSD([subQ1,subQ0]),TDD([makeQuery(id+"F11.boolean.opBoolean","SPLIT",EDGE,{"disambiguationData":[TD([subQ14])],"derivedFrom":subQ13})])]}),makeQuery(id+"F20.opExtrude","SWEPT_FACE",FACE,{"disambiguationData":[OSD([subQ1,subQ0]),TDD([makeQuery(id+"F11.boolean.opBoolean","SPLIT",EDGE,{"disambiguationData":[TD([subQ11])],"derivedFrom":subQ13})])]})]});}
            var sketch = newSketch(context, id + "F32", { "sketchPlane" : qUnion([Q0])});
            skLineSegment(sketch, "E25.bottom", {"start": v(324.64, -25) * mm, "end": v(274.64, -25) * mm, "construction": true});
            skLineSegment(sketch, "E25.top", {"start": v(324.64, 25) * mm, "end": v(274.64, 25) * mm, "construction": true});
            skLineSegment(sketch, "E25.left", {"start": v(324.64, -25) * mm, "end": v(324.64, 25) * mm, "construction": true});
            skLineSegment(sketch, "E25.right", {"start": v(274.64, -25) * mm, "end": v(274.64, 25) * mm, "construction": true});
            skPoint(sketch, "E25.middle", {"position": v(299.64, 0) * mm});
            skPoint(sketch, "E26", {"position": v(274.64, 25) * mm});
            skPoint(sketch, "E27", {"position": v(274.64, -25) * mm});
            skPoint(sketch, "E28", {"position": v(324.64, -25) * mm});
            skPoint(sketch, "E29", {"position": v(324.64, 25) * mm});
            skSolve(sketch);
        }
        {
            var Q0;
            Q0=sQuery(id+"F32.wireOp",VERTEX,"E26");
            var Q1;
            Q1=sQuery(id+"F32.wireOp",VERTEX,"E29");
            var Q2;
            Q2=sQuery(id+"F32.wireOp",VERTEX,"E28");
            var Q3;
            Q3=sQuery(id+"F32.wireOp",VERTEX,"E27");
            var Q4;
            Q4=makeQuery(id+"F1.opExtrude","SWEPT_BODY",BODY,{"disambiguationData":[OSD([sQuery(id+"F0.wireOp",EDGE,"E0.bottom"),sQuery(id+"F0.wireOp",EDGE,"E0.top"),sQuery(id+"F0.wireOp",EDGE,"E0.left"),sQuery(id+"F0.wireOp",EDGE,"E0.right")])]});
            hole(context, id + "F33", {"style" : HoleStyle.SIMPLE, "endStyle" : HoleEndStyle.BLIND, "standardTappedOrClearance" : lookupTablePath({ "standard" : "ISO", "engagement" : "75%", "pitch" : "0.8 mm", "size" : "M5", "type" : "Tapped" }), "standardBlindInLast" : lookupTablePath({ "standard" : "ISO", "engagement" : "75%", "pitch" : "0.8 mm", "size" : "M5", "type" : "Tapped" }), "holeDiameter" : 4.2 * mm, "showTappedDepth" : true, "holeDepth" : 9.68 * mm, "isTappedThrough" : true, "tappedDepth" : 7.28 * mm, "tapClearance" : 3, "locations" : qUnion([Q0, Q1, Q2, Q3]), "scope" : qUnion([Q4]), "majorDiameter" : 5 * mm});
        }
        {
            var Q0;
            Q0=makeQuery(id+"F9.boolean.opBoolean","COPY",FACE,{"derivedFrom":makeQuery(id+"F9.opExtrude","CAP_FACE",FACE,{"disambiguationData":[OSD([sQuery(id+"F7.wireOp",EDGE,"E3"),sQuery(id+"F7.wireOp",EDGE,"E4")])],"isStart":false})});
            var sketch = newSketch(context, id + "F34", { "sketchPlane" : qUnion([Q0])});
            skCircle(sketch, "E30.0", {"center": v(177.5, 0) * mm, "radius": 75 * mm});
            skCircle(sketch, "E31", {"center": v(177.5, 77.5) * mm, "radius": 1.5 * mm});
            skCircle(sketch, "E32.1.0", {"center": v(131.95, 62.7) * mm, "radius": 1.5 * mm});
            skCircle(sketch, "E32.2.0", {"center": v(103.8, 23.95) * mm, "radius": 1.5 * mm});
            skCircle(sketch, "E32.3.0", {"center": v(103.8, -23.95) * mm, "radius": 1.5 * mm});
            skCircle(sketch, "E32.4.0", {"center": v(131.95, -62.7) * mm, "radius": 1.5 * mm});
            skCircle(sketch, "E32.5.0", {"center": v(177.5, -77.5) * mm, "radius": 1.5 * mm});
            skCircle(sketch, "E32.6.0", {"center": v(223.05, -62.7) * mm, "radius": 1.5 * mm});
            skCircle(sketch, "E32.7.0", {"center": v(251.2, -23.95) * mm, "radius": 1.5 * mm});
            skCircle(sketch, "E32.8.0", {"center": v(251.2, 23.95) * mm, "radius": 1.5 * mm});
            skCircle(sketch, "E32.9.0", {"center": v(223.05, 62.7) * mm, "radius": 1.5 * mm});
            skSolve(sketch);
        }
        {
            var Q0;
            Q0 = qSketchRegion(id + "F34", true);
            extrude(context, id + "F35", {"entities" : qUnion([Q0]), "operationType" : NewBodyOperationType.REMOVE, "oppositeDirection" : true, "depth" : 3 * mm});
        }
    });
